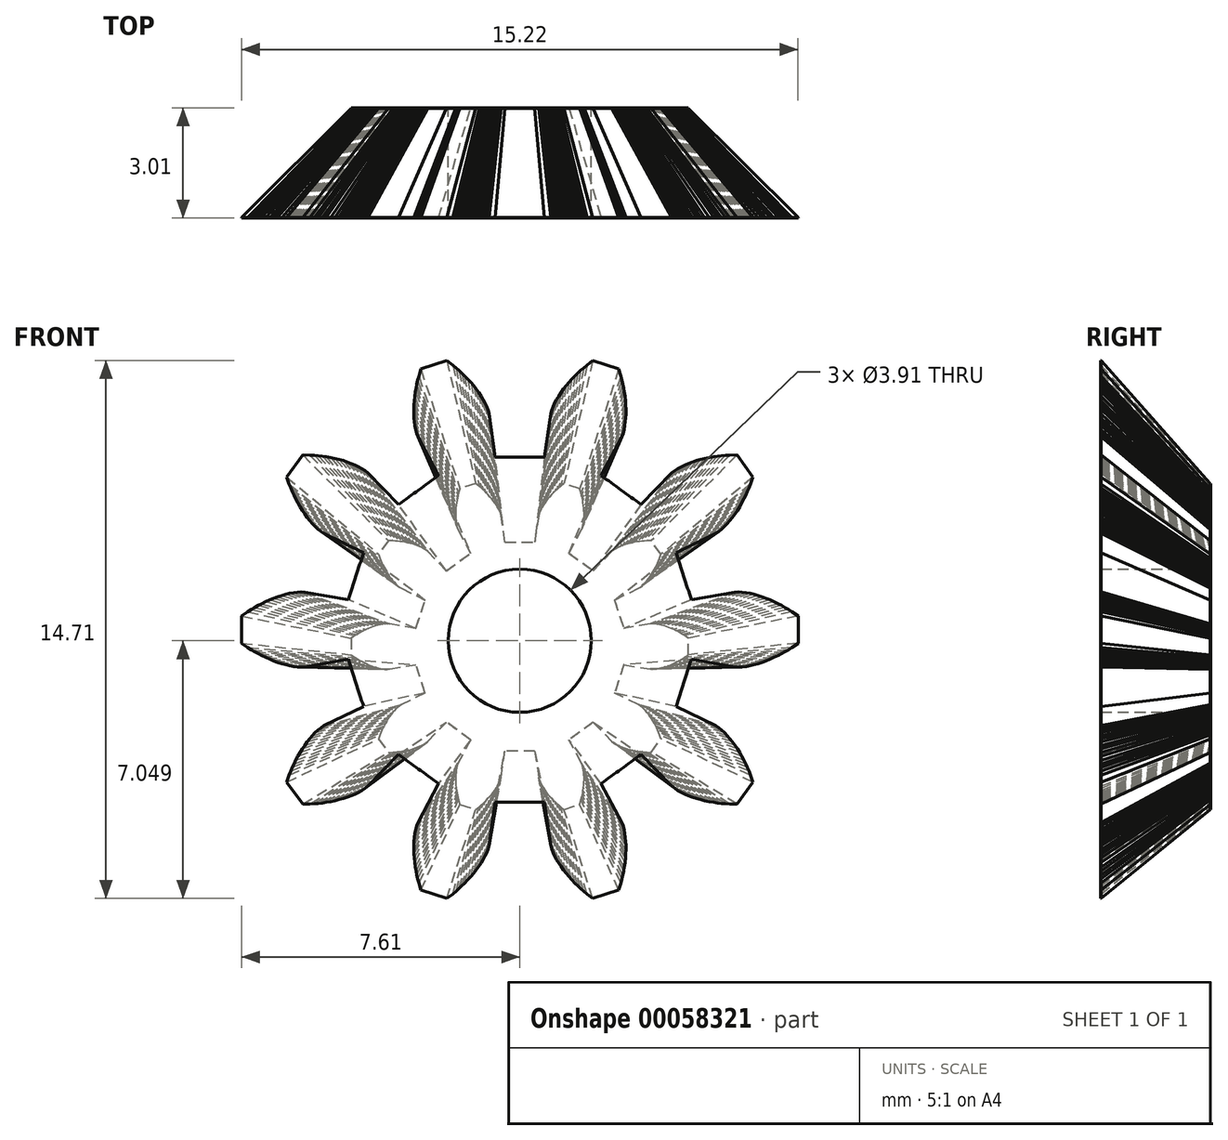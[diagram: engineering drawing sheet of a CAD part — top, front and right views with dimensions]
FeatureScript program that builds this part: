
annotation { "Feature Type Name" : "Feature", "Feature Type Description" : "" }
export const myFeature = defineFeature(function(context is Context, id is Id, definition is map)
    precondition{}
    {
        {
            var Q0;
            Q0=qCreatedBy(makeId("Front.planeOp"),FACE);
            var sketch = newSketch(context, id + "F0", { "sketchPlane" : qUnion([Q0])});
            skLineSegment(sketch, "E0", {"start": v(4.7, 0.36) * mm, "end": v(5.88, 0.15) * mm});
            skLineSegment(sketch, "E1", {"start": v(5.88, 0.15) * mm, "end": v(5.98, 0.15) * mm});
            skLineSegment(sketch, "E2", {"start": v(5.98, 0.15) * mm, "end": v(6.08, 0.15) * mm});
            skLineSegment(sketch, "E3", {"start": v(6.08, 0.15) * mm, "end": v(6.19, 0.17) * mm});
            skLineSegment(sketch, "E4", {"start": v(6.19, 0.17) * mm, "end": v(6.3, 0.19) * mm});
            skLineSegment(sketch, "E5", {"start": v(6.3, 0.19) * mm, "end": v(6.4, 0.2) * mm});
            skLineSegment(sketch, "E6", {"start": v(6.4, 0.2) * mm, "end": v(6.5, 0.24) * mm});
            skLineSegment(sketch, "E7", {"start": v(6.5, 0.24) * mm, "end": v(6.63, 0.28) * mm});
            skLineSegment(sketch, "E8", {"start": v(6.63, 0.28) * mm, "end": v(6.73, 0.32) * mm});
            skLineSegment(sketch, "E9", {"start": v(6.73, 0.32) * mm, "end": v(6.84, 0.36) * mm});
            skLineSegment(sketch, "E10", {"start": v(6.84, 0.36) * mm, "end": v(6.95, 0.4) * mm});
            skLineSegment(sketch, "E11", {"start": v(6.95, 0.4) * mm, "end": v(7.07, 0.47) * mm});
            skLineSegment(sketch, "E12", {"start": v(7.07, 0.47) * mm, "end": v(7.16, 0.52) * mm});
            skLineSegment(sketch, "E13", {"start": v(7.16, 0.52) * mm, "end": v(7.25, 0.57) * mm});
            skLineSegment(sketch, "E14", {"start": v(7.25, 0.57) * mm, "end": v(7.35, 0.63) * mm});
            skLineSegment(sketch, "E15", {"start": v(7.35, 0.63) * mm, "end": v(7.44, 0.69) * mm});
            skLineSegment(sketch, "E16", {"start": v(7.44, 0.69) * mm, "end": v(7.61, 0.8) * mm});
            skLineSegment(sketch, "E17", {"start": v(7.61, 0.8) * mm, "end": v(7.61, 1.55) * mm});
            skLineSegment(sketch, "E18", {"start": v(7.61, 1.55) * mm, "end": v(7.44, 1.66) * mm});
            skLineSegment(sketch, "E19", {"start": v(7.44, 1.66) * mm, "end": v(7.35, 1.72) * mm});
            skLineSegment(sketch, "E20", {"start": v(7.35, 1.72) * mm, "end": v(7.25, 1.78) * mm});
            skLineSegment(sketch, "E21", {"start": v(7.25, 1.78) * mm, "end": v(7.16, 1.83) * mm});
            skLineSegment(sketch, "E22", {"start": v(7.16, 1.83) * mm, "end": v(7.07, 1.88) * mm});
            skLineSegment(sketch, "E23", {"start": v(7.07, 1.88) * mm, "end": v(6.95, 1.94) * mm});
            skLineSegment(sketch, "E24", {"start": v(6.95, 1.94) * mm, "end": v(6.84, 1.99) * mm});
            skLineSegment(sketch, "E25", {"start": v(6.84, 1.99) * mm, "end": v(6.73, 2.03) * mm});
            skLineSegment(sketch, "E26", {"start": v(6.73, 2.03) * mm, "end": v(6.63, 2.07) * mm});
            skLineSegment(sketch, "E27", {"start": v(6.63, 2.07) * mm, "end": v(6.5, 2.1) * mm});
            skLineSegment(sketch, "E28", {"start": v(6.5, 2.1) * mm, "end": v(6.4, 2.14) * mm});
            skLineSegment(sketch, "E29", {"start": v(6.4, 2.14) * mm, "end": v(6.3, 2.16) * mm});
            skLineSegment(sketch, "E30", {"start": v(6.3, 2.16) * mm, "end": v(6.19, 2.18) * mm});
            skLineSegment(sketch, "E31", {"start": v(6.19, 2.18) * mm, "end": v(6.08, 2.2) * mm});
            skLineSegment(sketch, "E32", {"start": v(6.08, 2.2) * mm, "end": v(5.98, 2.2) * mm});
            skLineSegment(sketch, "E33", {"start": v(5.98, 2.2) * mm, "end": v(5.88, 2.2) * mm});
            skLineSegment(sketch, "E34", {"start": v(5.88, 2.2) * mm, "end": v(4.7, 1.99) * mm});
            skArc(sketch, "E35", {"start": v(4.7, 1.99) * mm, "mid": v(4.48, 2.63) * mm, "end": v(4.28, 3.27) * mm});
            skLineSegment(sketch, "E36", {"start": v(4.28, 3.27) * mm, "end": v(5.36, 3.8) * mm});
            skLineSegment(sketch, "E37", {"start": v(5.36, 3.8) * mm, "end": v(5.44, 3.86) * mm});
            skLineSegment(sketch, "E38", {"start": v(5.44, 3.86) * mm, "end": v(5.52, 3.92) * mm});
            skLineSegment(sketch, "E39", {"start": v(5.52, 3.92) * mm, "end": v(5.6, 4) * mm});
            skLineSegment(sketch, "E40", {"start": v(5.6, 4) * mm, "end": v(5.67, 4.08) * mm});
            skLineSegment(sketch, "E41", {"start": v(5.67, 4.08) * mm, "end": v(5.74, 4.15) * mm});
            skLineSegment(sketch, "E42", {"start": v(5.74, 4.15) * mm, "end": v(5.81, 4.24) * mm});
            skLineSegment(sketch, "E43", {"start": v(5.81, 4.24) * mm, "end": v(5.89, 4.34) * mm});
            skLineSegment(sketch, "E44", {"start": v(5.89, 4.34) * mm, "end": v(5.95, 4.44) * mm});
            skLineSegment(sketch, "E45", {"start": v(5.95, 4.44) * mm, "end": v(6.01, 4.53) * mm});
            skLineSegment(sketch, "E46", {"start": v(6.01, 4.53) * mm, "end": v(6.07, 4.64) * mm});
            skLineSegment(sketch, "E47", {"start": v(6.07, 4.64) * mm, "end": v(6.13, 4.76) * mm});
            skLineSegment(sketch, "E48", {"start": v(6.13, 4.76) * mm, "end": v(6.18, 4.85) * mm});
            skLineSegment(sketch, "E49", {"start": v(6.18, 4.85) * mm, "end": v(6.22, 4.95) * mm});
            skLineSegment(sketch, "E50", {"start": v(6.22, 4.95) * mm, "end": v(6.27, 5.05) * mm});
            skLineSegment(sketch, "E51", {"start": v(6.27, 5.05) * mm, "end": v(6.3, 5.16) * mm});
            skLineSegment(sketch, "E52", {"start": v(6.3, 5.16) * mm, "end": v(6.38, 5.35) * mm});
            skLineSegment(sketch, "E53", {"start": v(6.38, 5.35) * mm, "end": v(5.94, 5.95) * mm});
            skLineSegment(sketch, "E54", {"start": v(5.94, 5.95) * mm, "end": v(5.74, 5.94) * mm});
            skLineSegment(sketch, "E55", {"start": v(5.74, 5.94) * mm, "end": v(5.62, 5.94) * mm});
            skLineSegment(sketch, "E56", {"start": v(5.62, 5.94) * mm, "end": v(5.51, 5.93) * mm});
            skLineSegment(sketch, "E57", {"start": v(5.51, 5.93) * mm, "end": v(5.4, 5.92) * mm});
            skLineSegment(sketch, "E58", {"start": v(5.4, 5.92) * mm, "end": v(5.3, 5.9) * mm});
            skLineSegment(sketch, "E59", {"start": v(5.3, 5.9) * mm, "end": v(5.17, 5.88) * mm});
            skLineSegment(sketch, "E60", {"start": v(5.17, 5.88) * mm, "end": v(5.05, 5.85) * mm});
            skLineSegment(sketch, "E61", {"start": v(5.05, 5.85) * mm, "end": v(4.94, 5.83) * mm});
            skLineSegment(sketch, "E62", {"start": v(4.94, 5.83) * mm, "end": v(4.83, 5.8) * mm});
            skLineSegment(sketch, "E63", {"start": v(4.83, 5.8) * mm, "end": v(4.71, 5.76) * mm});
            skLineSegment(sketch, "E64", {"start": v(4.71, 5.76) * mm, "end": v(4.6, 5.72) * mm});
            skLineSegment(sketch, "E65", {"start": v(4.6, 5.72) * mm, "end": v(4.51, 5.68) * mm});
            skLineSegment(sketch, "E66", {"start": v(4.51, 5.68) * mm, "end": v(4.41, 5.63) * mm});
            skLineSegment(sketch, "E67", {"start": v(4.41, 5.63) * mm, "end": v(4.32, 5.58) * mm});
            skLineSegment(sketch, "E68", {"start": v(4.32, 5.58) * mm, "end": v(4.23, 5.52) * mm});
            skLineSegment(sketch, "E69", {"start": v(4.23, 5.52) * mm, "end": v(4.16, 5.46) * mm});
            skLineSegment(sketch, "E70", {"start": v(4.16, 5.46) * mm, "end": v(3.32, 4.6) * mm});
            skArc(sketch, "E71", {"start": v(3.32, 4.6) * mm, "mid": v(2.77, 4.99) * mm, "end": v(2.23, 5.39) * mm});
            skLineSegment(sketch, "E72", {"start": v(2.23, 5.39) * mm, "end": v(2.79, 6.45) * mm});
            skLineSegment(sketch, "E73", {"start": v(2.79, 6.45) * mm, "end": v(2.82, 6.54) * mm});
            skLineSegment(sketch, "E74", {"start": v(2.82, 6.54) * mm, "end": v(2.85, 6.64) * mm});
            skLineSegment(sketch, "E75", {"start": v(2.85, 6.64) * mm, "end": v(2.87, 6.75) * mm});
            skLineSegment(sketch, "E76", {"start": v(2.87, 6.75) * mm, "end": v(2.89, 6.86) * mm});
            skLineSegment(sketch, "E77", {"start": v(2.89, 6.86) * mm, "end": v(2.9, 6.96) * mm});
            skLineSegment(sketch, "E78", {"start": v(2.9, 6.96) * mm, "end": v(2.9, 7.07) * mm});
            skLineSegment(sketch, "E79", {"start": v(2.9, 7.07) * mm, "end": v(2.9, 7.2) * mm});
            skLineSegment(sketch, "E80", {"start": v(2.9, 7.2) * mm, "end": v(2.9, 7.3) * mm});
            skLineSegment(sketch, "E81", {"start": v(2.9, 7.3) * mm, "end": v(2.89, 7.43) * mm});
            skLineSegment(sketch, "E82", {"start": v(2.89, 7.43) * mm, "end": v(2.87, 7.55) * mm});
            skLineSegment(sketch, "E83", {"start": v(2.87, 7.55) * mm, "end": v(2.86, 7.68) * mm});
            skLineSegment(sketch, "E84", {"start": v(2.86, 7.68) * mm, "end": v(2.84, 7.78) * mm});
            skLineSegment(sketch, "E85", {"start": v(2.84, 7.78) * mm, "end": v(2.82, 7.88) * mm});
            skLineSegment(sketch, "E86", {"start": v(2.82, 7.88) * mm, "end": v(2.8, 8) * mm});
            skLineSegment(sketch, "E87", {"start": v(2.8, 8) * mm, "end": v(2.76, 8.1) * mm});
            skLineSegment(sketch, "E88", {"start": v(2.76, 8.1) * mm, "end": v(2.7, 8.3) * mm});
            skLineSegment(sketch, "E89", {"start": v(2.7, 8.3) * mm, "end": v(2, 8.53) * mm});
            skLineSegment(sketch, "E90", {"start": v(2, 8.53) * mm, "end": v(1.84, 8.4) * mm});
            skLineSegment(sketch, "E91", {"start": v(1.84, 8.4) * mm, "end": v(1.75, 8.33) * mm});
            skLineSegment(sketch, "E92", {"start": v(1.75, 8.33) * mm, "end": v(1.66, 8.26) * mm});
            skLineSegment(sketch, "E93", {"start": v(1.66, 8.26) * mm, "end": v(1.59, 8.19) * mm});
            skLineSegment(sketch, "E94", {"start": v(1.59, 8.19) * mm, "end": v(1.51, 8.11) * mm});
            skLineSegment(sketch, "E95", {"start": v(1.51, 8.11) * mm, "end": v(1.42, 8.02) * mm});
            skLineSegment(sketch, "E96", {"start": v(1.42, 8.02) * mm, "end": v(1.34, 7.93) * mm});
            skLineSegment(sketch, "E97", {"start": v(1.34, 7.93) * mm, "end": v(1.26, 7.84) * mm});
            skLineSegment(sketch, "E98", {"start": v(1.26, 7.84) * mm, "end": v(1.2, 7.75) * mm});
            skLineSegment(sketch, "E99", {"start": v(1.2, 7.75) * mm, "end": v(1.12, 7.65) * mm});
            skLineSegment(sketch, "E100", {"start": v(1.12, 7.65) * mm, "end": v(1.06, 7.56) * mm});
            skLineSegment(sketch, "E101", {"start": v(1.06, 7.56) * mm, "end": v(1, 7.47) * mm});
            skLineSegment(sketch, "E102", {"start": v(1, 7.47) * mm, "end": v(0.95, 7.37) * mm});
            skLineSegment(sketch, "E103", {"start": v(0.95, 7.37) * mm, "end": v(0.9, 7.28) * mm});
            skLineSegment(sketch, "E104", {"start": v(0.9, 7.28) * mm, "end": v(0.87, 7.18) * mm});
            skLineSegment(sketch, "E105", {"start": v(0.87, 7.18) * mm, "end": v(0.85, 7.08) * mm});
            skLineSegment(sketch, "E106", {"start": v(0.85, 7.08) * mm, "end": v(0.67, 5.89) * mm});
            skArc(sketch, "E107", {"start": v(0.67, 5.89) * mm, "mid": v(0, 5.89) * mm, "end": v(-0.67, 5.89) * mm});
            skLineSegment(sketch, "E108", {"start": v(-0.67, 5.89) * mm, "end": v(-0.85, 7.08) * mm});
            skLineSegment(sketch, "E109", {"start": v(-0.85, 7.08) * mm, "end": v(-0.87, 7.18) * mm});
            skLineSegment(sketch, "E110", {"start": v(-0.87, 7.18) * mm, "end": v(-0.9, 7.28) * mm});
            skLineSegment(sketch, "E111", {"start": v(-0.9, 7.28) * mm, "end": v(-0.95, 7.37) * mm});
            skLineSegment(sketch, "E112", {"start": v(-0.95, 7.37) * mm, "end": v(-1, 7.47) * mm});
            skLineSegment(sketch, "E113", {"start": v(-1, 7.47) * mm, "end": v(-1.06, 7.56) * mm});
            skLineSegment(sketch, "E114", {"start": v(-1.06, 7.56) * mm, "end": v(-1.12, 7.65) * mm});
            skLineSegment(sketch, "E115", {"start": v(-1.12, 7.65) * mm, "end": v(-1.2, 7.75) * mm});
            skLineSegment(sketch, "E116", {"start": v(-1.2, 7.75) * mm, "end": v(-1.26, 7.84) * mm});
            skLineSegment(sketch, "E117", {"start": v(-1.26, 7.84) * mm, "end": v(-1.34, 7.93) * mm});
            skLineSegment(sketch, "E118", {"start": v(-1.34, 7.93) * mm, "end": v(-1.42, 8.02) * mm});
            skLineSegment(sketch, "E119", {"start": v(-1.42, 8.02) * mm, "end": v(-1.51, 8.11) * mm});
            skLineSegment(sketch, "E120", {"start": v(-1.51, 8.11) * mm, "end": v(-1.59, 8.19) * mm});
            skLineSegment(sketch, "E121", {"start": v(-1.59, 8.19) * mm, "end": v(-1.66, 8.26) * mm});
            skLineSegment(sketch, "E122", {"start": v(-1.66, 8.26) * mm, "end": v(-1.75, 8.33) * mm});
            skLineSegment(sketch, "E123", {"start": v(-1.75, 8.33) * mm, "end": v(-1.84, 8.4) * mm});
            skLineSegment(sketch, "E124", {"start": v(-1.84, 8.4) * mm, "end": v(-2, 8.53) * mm});
            skLineSegment(sketch, "E125", {"start": v(-2, 8.53) * mm, "end": v(-2.7, 8.3) * mm});
            skLineSegment(sketch, "E126", {"start": v(-2.7, 8.3) * mm, "end": v(-2.76, 8.1) * mm});
            skLineSegment(sketch, "E127", {"start": v(-2.76, 8.1) * mm, "end": v(-2.8, 8) * mm});
            skLineSegment(sketch, "E128", {"start": v(-2.8, 8) * mm, "end": v(-2.82, 7.88) * mm});
            skLineSegment(sketch, "E129", {"start": v(-2.82, 7.88) * mm, "end": v(-2.84, 7.78) * mm});
            skLineSegment(sketch, "E130", {"start": v(-2.84, 7.78) * mm, "end": v(-2.86, 7.68) * mm});
            skLineSegment(sketch, "E131", {"start": v(-2.86, 7.68) * mm, "end": v(-2.87, 7.55) * mm});
            skLineSegment(sketch, "E132", {"start": v(-2.87, 7.55) * mm, "end": v(-2.89, 7.43) * mm});
            skLineSegment(sketch, "E133", {"start": v(-2.89, 7.43) * mm, "end": v(-2.9, 7.3) * mm});
            skLineSegment(sketch, "E134", {"start": v(-2.9, 7.3) * mm, "end": v(-2.9, 7.2) * mm});
            skLineSegment(sketch, "E135", {"start": v(-2.9, 7.2) * mm, "end": v(-2.9, 7.07) * mm});
            skLineSegment(sketch, "E136", {"start": v(-2.9, 7.07) * mm, "end": v(-2.9, 6.96) * mm});
            skLineSegment(sketch, "E137", {"start": v(-2.9, 6.96) * mm, "end": v(-2.89, 6.86) * mm});
            skLineSegment(sketch, "E138", {"start": v(-2.89, 6.86) * mm, "end": v(-2.87, 6.75) * mm});
            skLineSegment(sketch, "E139", {"start": v(-2.87, 6.75) * mm, "end": v(-2.85, 6.64) * mm});
            skLineSegment(sketch, "E140", {"start": v(-2.85, 6.64) * mm, "end": v(-2.82, 6.54) * mm});
            skLineSegment(sketch, "E141", {"start": v(-2.82, 6.54) * mm, "end": v(-2.79, 6.45) * mm});
            skLineSegment(sketch, "E142", {"start": v(-2.79, 6.45) * mm, "end": v(-2.23, 5.39) * mm});
            skArc(sketch, "E143", {"start": v(-2.23, 5.39) * mm, "mid": v(-2.77, 4.99) * mm, "end": v(-3.32, 4.6) * mm});
            skLineSegment(sketch, "E144", {"start": v(-3.32, 4.6) * mm, "end": v(-4.16, 5.46) * mm});
            skLineSegment(sketch, "E145", {"start": v(-4.16, 5.46) * mm, "end": v(-4.23, 5.52) * mm});
            skLineSegment(sketch, "E146", {"start": v(-4.23, 5.52) * mm, "end": v(-4.32, 5.58) * mm});
            skLineSegment(sketch, "E147", {"start": v(-4.32, 5.58) * mm, "end": v(-4.41, 5.63) * mm});
            skLineSegment(sketch, "E148", {"start": v(-4.41, 5.63) * mm, "end": v(-4.51, 5.68) * mm});
            skLineSegment(sketch, "E149", {"start": v(-4.51, 5.68) * mm, "end": v(-4.6, 5.72) * mm});
            skLineSegment(sketch, "E150", {"start": v(-4.6, 5.72) * mm, "end": v(-4.71, 5.76) * mm});
            skLineSegment(sketch, "E151", {"start": v(-4.71, 5.76) * mm, "end": v(-4.83, 5.8) * mm});
            skLineSegment(sketch, "E152", {"start": v(-4.83, 5.8) * mm, "end": v(-4.94, 5.83) * mm});
            skLineSegment(sketch, "E153", {"start": v(-4.94, 5.83) * mm, "end": v(-5.05, 5.85) * mm});
            skLineSegment(sketch, "E154", {"start": v(-5.05, 5.85) * mm, "end": v(-5.17, 5.88) * mm});
            skLineSegment(sketch, "E155", {"start": v(-5.17, 5.88) * mm, "end": v(-5.3, 5.9) * mm});
            skLineSegment(sketch, "E156", {"start": v(-5.3, 5.9) * mm, "end": v(-5.4, 5.92) * mm});
            skLineSegment(sketch, "E157", {"start": v(-5.4, 5.92) * mm, "end": v(-5.51, 5.93) * mm});
            skLineSegment(sketch, "E158", {"start": v(-5.51, 5.93) * mm, "end": v(-5.62, 5.94) * mm});
            skLineSegment(sketch, "E159", {"start": v(-5.62, 5.94) * mm, "end": v(-5.74, 5.94) * mm});
            skLineSegment(sketch, "E160", {"start": v(-5.74, 5.94) * mm, "end": v(-5.94, 5.95) * mm});
            skLineSegment(sketch, "E161", {"start": v(-5.94, 5.95) * mm, "end": v(-6.38, 5.35) * mm});
            skLineSegment(sketch, "E162", {"start": v(-6.38, 5.35) * mm, "end": v(-6.3, 5.16) * mm});
            skLineSegment(sketch, "E163", {"start": v(-6.3, 5.16) * mm, "end": v(-6.27, 5.05) * mm});
            skLineSegment(sketch, "E164", {"start": v(-6.27, 5.05) * mm, "end": v(-6.22, 4.95) * mm});
            skLineSegment(sketch, "E165", {"start": v(-6.22, 4.95) * mm, "end": v(-6.18, 4.85) * mm});
            skLineSegment(sketch, "E166", {"start": v(-6.18, 4.85) * mm, "end": v(-6.13, 4.76) * mm});
            skLineSegment(sketch, "E167", {"start": v(-6.13, 4.76) * mm, "end": v(-6.07, 4.64) * mm});
            skLineSegment(sketch, "E168", {"start": v(-6.07, 4.64) * mm, "end": v(-6.01, 4.53) * mm});
            skLineSegment(sketch, "E169", {"start": v(-6.01, 4.53) * mm, "end": v(-5.95, 4.44) * mm});
            skLineSegment(sketch, "E170", {"start": v(-5.95, 4.44) * mm, "end": v(-5.89, 4.34) * mm});
            skLineSegment(sketch, "E171", {"start": v(-5.89, 4.34) * mm, "end": v(-5.81, 4.24) * mm});
            skLineSegment(sketch, "E172", {"start": v(-5.81, 4.24) * mm, "end": v(-5.74, 4.15) * mm});
            skLineSegment(sketch, "E173", {"start": v(-5.74, 4.15) * mm, "end": v(-5.67, 4.08) * mm});
            skLineSegment(sketch, "E174", {"start": v(-5.67, 4.08) * mm, "end": v(-5.6, 4) * mm});
            skLineSegment(sketch, "E175", {"start": v(-5.6, 4) * mm, "end": v(-5.52, 3.92) * mm});
            skLineSegment(sketch, "E176", {"start": v(-5.52, 3.92) * mm, "end": v(-5.44, 3.86) * mm});
            skLineSegment(sketch, "E177", {"start": v(-5.44, 3.86) * mm, "end": v(-5.36, 3.8) * mm});
            skLineSegment(sketch, "E178", {"start": v(-5.36, 3.8) * mm, "end": v(-4.28, 3.27) * mm});
            skArc(sketch, "E179", {"start": v(-4.28, 3.27) * mm, "mid": v(-4.48, 2.63) * mm, "end": v(-4.7, 1.99) * mm});
            skLineSegment(sketch, "E180", {"start": v(-4.7, 1.99) * mm, "end": v(-5.88, 2.2) * mm});
            skLineSegment(sketch, "E181", {"start": v(-5.88, 2.2) * mm, "end": v(-5.98, 2.2) * mm});
            skLineSegment(sketch, "E182", {"start": v(-5.98, 2.2) * mm, "end": v(-6.08, 2.2) * mm});
            skLineSegment(sketch, "E183", {"start": v(-6.08, 2.2) * mm, "end": v(-6.19, 2.18) * mm});
            skLineSegment(sketch, "E184", {"start": v(-6.19, 2.18) * mm, "end": v(-6.3, 2.16) * mm});
            skLineSegment(sketch, "E185", {"start": v(-6.3, 2.16) * mm, "end": v(-6.4, 2.14) * mm});
            skLineSegment(sketch, "E186", {"start": v(-6.4, 2.14) * mm, "end": v(-6.5, 2.1) * mm});
            skLineSegment(sketch, "E187", {"start": v(-6.5, 2.1) * mm, "end": v(-6.63, 2.07) * mm});
            skLineSegment(sketch, "E188", {"start": v(-6.63, 2.07) * mm, "end": v(-6.73, 2.03) * mm});
            skLineSegment(sketch, "E189", {"start": v(-6.73, 2.03) * mm, "end": v(-6.84, 1.99) * mm});
            skLineSegment(sketch, "E190", {"start": v(-6.84, 1.99) * mm, "end": v(-6.95, 1.94) * mm});
            skLineSegment(sketch, "E191", {"start": v(-6.95, 1.94) * mm, "end": v(-7.07, 1.88) * mm});
            skLineSegment(sketch, "E192", {"start": v(-7.07, 1.88) * mm, "end": v(-7.16, 1.83) * mm});
            skLineSegment(sketch, "E193", {"start": v(-7.16, 1.83) * mm, "end": v(-7.25, 1.78) * mm});
            skLineSegment(sketch, "E194", {"start": v(-7.25, 1.78) * mm, "end": v(-7.35, 1.72) * mm});
            skLineSegment(sketch, "E195", {"start": v(-7.35, 1.72) * mm, "end": v(-7.44, 1.66) * mm});
            skLineSegment(sketch, "E196", {"start": v(-7.44, 1.66) * mm, "end": v(-7.61, 1.55) * mm});
            skLineSegment(sketch, "E197", {"start": v(-7.61, 1.55) * mm, "end": v(-7.61, 0.8) * mm});
            skLineSegment(sketch, "E198", {"start": v(-7.61, 0.8) * mm, "end": v(-7.44, 0.69) * mm});
            skLineSegment(sketch, "E199", {"start": v(-7.44, 0.69) * mm, "end": v(-7.35, 0.63) * mm});
            skLineSegment(sketch, "E200", {"start": v(-7.35, 0.63) * mm, "end": v(-7.25, 0.57) * mm});
            skLineSegment(sketch, "E201", {"start": v(-7.25, 0.57) * mm, "end": v(-7.16, 0.52) * mm});
            skLineSegment(sketch, "E202", {"start": v(-7.16, 0.52) * mm, "end": v(-7.07, 0.47) * mm});
            skLineSegment(sketch, "E203", {"start": v(-7.07, 0.47) * mm, "end": v(-6.95, 0.4) * mm});
            skLineSegment(sketch, "E204", {"start": v(-6.95, 0.4) * mm, "end": v(-6.84, 0.36) * mm});
            skLineSegment(sketch, "E205", {"start": v(-6.84, 0.36) * mm, "end": v(-6.73, 0.32) * mm});
            skLineSegment(sketch, "E206", {"start": v(-6.73, 0.32) * mm, "end": v(-6.63, 0.28) * mm});
            skLineSegment(sketch, "E207", {"start": v(-6.63, 0.28) * mm, "end": v(-6.5, 0.24) * mm});
            skLineSegment(sketch, "E208", {"start": v(-6.5, 0.24) * mm, "end": v(-6.4, 0.2) * mm});
            skLineSegment(sketch, "E209", {"start": v(-6.4, 0.2) * mm, "end": v(-6.3, 0.19) * mm});
            skLineSegment(sketch, "E210", {"start": v(-6.3, 0.19) * mm, "end": v(-6.19, 0.17) * mm});
            skLineSegment(sketch, "E211", {"start": v(-6.19, 0.17) * mm, "end": v(-6.08, 0.15) * mm});
            skLineSegment(sketch, "E212", {"start": v(-6.08, 0.15) * mm, "end": v(-5.98, 0.15) * mm});
            skLineSegment(sketch, "E213", {"start": v(-5.98, 0.15) * mm, "end": v(-5.88, 0.15) * mm});
            skLineSegment(sketch, "E214", {"start": v(-5.88, 0.15) * mm, "end": v(-4.7, 0.36) * mm});
            skArc(sketch, "E215", {"start": v(-4.7, 0.36) * mm, "mid": v(-4.48, -0.28) * mm, "end": v(-4.28, -0.92) * mm});
            skLineSegment(sketch, "E216", {"start": v(-4.28, -0.92) * mm, "end": v(-5.36, -1.45) * mm});
            skLineSegment(sketch, "E217", {"start": v(-5.36, -1.45) * mm, "end": v(-5.44, -1.5) * mm});
            skLineSegment(sketch, "E218", {"start": v(-5.44, -1.5) * mm, "end": v(-5.52, -1.57) * mm});
            skLineSegment(sketch, "E219", {"start": v(-5.52, -1.57) * mm, "end": v(-5.6, -1.65) * mm});
            skLineSegment(sketch, "E220", {"start": v(-5.6, -1.65) * mm, "end": v(-5.67, -1.73) * mm});
            skLineSegment(sketch, "E221", {"start": v(-5.67, -1.73) * mm, "end": v(-5.74, -1.8) * mm});
            skLineSegment(sketch, "E222", {"start": v(-5.74, -1.8) * mm, "end": v(-5.81, -1.9) * mm});
            skLineSegment(sketch, "E223", {"start": v(-5.81, -1.9) * mm, "end": v(-5.89, -2) * mm});
            skLineSegment(sketch, "E224", {"start": v(-5.89, -2) * mm, "end": v(-5.95, -2.09) * mm});
            skLineSegment(sketch, "E225", {"start": v(-5.95, -2.09) * mm, "end": v(-6.01, -2.18) * mm});
            skLineSegment(sketch, "E226", {"start": v(-6.01, -2.18) * mm, "end": v(-6.07, -2.3) * mm});
            skLineSegment(sketch, "E227", {"start": v(-6.07, -2.3) * mm, "end": v(-6.13, -2.4) * mm});
            skLineSegment(sketch, "E228", {"start": v(-6.13, -2.4) * mm, "end": v(-6.18, -2.5) * mm});
            skLineSegment(sketch, "E229", {"start": v(-6.18, -2.5) * mm, "end": v(-6.22, -2.6) * mm});
            skLineSegment(sketch, "E230", {"start": v(-6.22, -2.6) * mm, "end": v(-6.27, -2.7) * mm});
            skLineSegment(sketch, "E231", {"start": v(-6.27, -2.7) * mm, "end": v(-6.3, -2.8) * mm});
            skLineSegment(sketch, "E232", {"start": v(-6.3, -2.8) * mm, "end": v(-6.38, -3) * mm});
            skLineSegment(sketch, "E233", {"start": v(-6.38, -3) * mm, "end": v(-5.94, -3.6) * mm});
            skLineSegment(sketch, "E234", {"start": v(-5.94, -3.6) * mm, "end": v(-5.74, -3.6) * mm});
            skLineSegment(sketch, "E235", {"start": v(-5.74, -3.6) * mm, "end": v(-5.62, -3.59) * mm});
            skLineSegment(sketch, "E236", {"start": v(-5.62, -3.59) * mm, "end": v(-5.51, -3.58) * mm});
            skLineSegment(sketch, "E237", {"start": v(-5.51, -3.58) * mm, "end": v(-5.4, -3.57) * mm});
            skLineSegment(sketch, "E238", {"start": v(-5.4, -3.57) * mm, "end": v(-5.3, -3.55) * mm});
            skLineSegment(sketch, "E239", {"start": v(-5.3, -3.55) * mm, "end": v(-5.17, -3.53) * mm});
            skLineSegment(sketch, "E240", {"start": v(-5.17, -3.53) * mm, "end": v(-5.05, -3.5) * mm});
            skLineSegment(sketch, "E241", {"start": v(-5.05, -3.5) * mm, "end": v(-4.94, -3.48) * mm});
            skLineSegment(sketch, "E242", {"start": v(-4.94, -3.48) * mm, "end": v(-4.83, -3.45) * mm});
            skLineSegment(sketch, "E243", {"start": v(-4.83, -3.45) * mm, "end": v(-4.71, -3.4) * mm});
            skLineSegment(sketch, "E244", {"start": v(-4.71, -3.4) * mm, "end": v(-4.6, -3.37) * mm});
            skLineSegment(sketch, "E245", {"start": v(-4.6, -3.37) * mm, "end": v(-4.51, -3.33) * mm});
            skLineSegment(sketch, "E246", {"start": v(-4.51, -3.33) * mm, "end": v(-4.41, -3.28) * mm});
            skLineSegment(sketch, "E247", {"start": v(-4.41, -3.28) * mm, "end": v(-4.32, -3.23) * mm});
            skLineSegment(sketch, "E248", {"start": v(-4.32, -3.23) * mm, "end": v(-4.23, -3.17) * mm});
            skLineSegment(sketch, "E249", {"start": v(-4.23, -3.17) * mm, "end": v(-4.16, -3.1) * mm});
            skLineSegment(sketch, "E250", {"start": v(-4.16, -3.1) * mm, "end": v(-3.32, -2.24) * mm});
            skArc(sketch, "E251", {"start": v(-3.32, -2.24) * mm, "mid": v(-2.77, -2.64) * mm, "end": v(-2.23, -3.04) * mm});
            skLineSegment(sketch, "E252", {"start": v(-2.23, -3.04) * mm, "end": v(-2.79, -4.1) * mm});
            skLineSegment(sketch, "E253", {"start": v(-2.79, -4.1) * mm, "end": v(-2.82, -4.2) * mm});
            skLineSegment(sketch, "E254", {"start": v(-2.82, -4.2) * mm, "end": v(-2.85, -4.3) * mm});
            skLineSegment(sketch, "E255", {"start": v(-2.85, -4.3) * mm, "end": v(-2.87, -4.4) * mm});
            skLineSegment(sketch, "E256", {"start": v(-2.87, -4.4) * mm, "end": v(-2.89, -4.5) * mm});
            skLineSegment(sketch, "E257", {"start": v(-2.89, -4.5) * mm, "end": v(-2.9, -4.61) * mm});
            skLineSegment(sketch, "E258", {"start": v(-2.9, -4.61) * mm, "end": v(-2.9, -4.73) * mm});
            skLineSegment(sketch, "E259", {"start": v(-2.9, -4.73) * mm, "end": v(-2.9, -4.85) * mm});
            skLineSegment(sketch, "E260", {"start": v(-2.9, -4.85) * mm, "end": v(-2.9, -4.96) * mm});
            skLineSegment(sketch, "E261", {"start": v(-2.9, -4.96) * mm, "end": v(-2.89, -5.08) * mm});
            skLineSegment(sketch, "E262", {"start": v(-2.89, -5.08) * mm, "end": v(-2.87, -5.2) * mm});
            skLineSegment(sketch, "E263", {"start": v(-2.87, -5.2) * mm, "end": v(-2.86, -5.33) * mm});
            skLineSegment(sketch, "E264", {"start": v(-2.86, -5.33) * mm, "end": v(-2.84, -5.43) * mm});
            skLineSegment(sketch, "E265", {"start": v(-2.84, -5.43) * mm, "end": v(-2.82, -5.54) * mm});
            skLineSegment(sketch, "E266", {"start": v(-2.82, -5.54) * mm, "end": v(-2.8, -5.64) * mm});
            skLineSegment(sketch, "E267", {"start": v(-2.8, -5.64) * mm, "end": v(-2.76, -5.76) * mm});
            skLineSegment(sketch, "E268", {"start": v(-2.76, -5.76) * mm, "end": v(-2.7, -5.95) * mm});
            skLineSegment(sketch, "E269", {"start": v(-2.7, -5.95) * mm, "end": v(-2, -6.18) * mm});
            skLineSegment(sketch, "E270", {"start": v(-2, -6.18) * mm, "end": v(-1.84, -6.06) * mm});
            skLineSegment(sketch, "E271", {"start": v(-1.84, -6.06) * mm, "end": v(-1.75, -5.98) * mm});
            skLineSegment(sketch, "E272", {"start": v(-1.75, -5.98) * mm, "end": v(-1.66, -5.9) * mm});
            skLineSegment(sketch, "E273", {"start": v(-1.66, -5.9) * mm, "end": v(-1.59, -5.84) * mm});
            skLineSegment(sketch, "E274", {"start": v(-1.59, -5.84) * mm, "end": v(-1.51, -5.77) * mm});
            skLineSegment(sketch, "E275", {"start": v(-1.51, -5.77) * mm, "end": v(-1.42, -5.67) * mm});
            skLineSegment(sketch, "E276", {"start": v(-1.42, -5.67) * mm, "end": v(-1.34, -5.58) * mm});
            skLineSegment(sketch, "E277", {"start": v(-1.34, -5.58) * mm, "end": v(-1.26, -5.5) * mm});
            skLineSegment(sketch, "E278", {"start": v(-1.26, -5.5) * mm, "end": v(-1.2, -5.4) * mm});
            skLineSegment(sketch, "E279", {"start": v(-1.2, -5.4) * mm, "end": v(-1.12, -5.3) * mm});
            skLineSegment(sketch, "E280", {"start": v(-1.12, -5.3) * mm, "end": v(-1.06, -5.2) * mm});
            skLineSegment(sketch, "E281", {"start": v(-1.06, -5.2) * mm, "end": v(-1, -5.12) * mm});
            skLineSegment(sketch, "E282", {"start": v(-1, -5.12) * mm, "end": v(-0.95, -5.02) * mm});
            skLineSegment(sketch, "E283", {"start": v(-0.95, -5.02) * mm, "end": v(-0.9, -4.93) * mm});
            skLineSegment(sketch, "E284", {"start": v(-0.9, -4.93) * mm, "end": v(-0.87, -4.83) * mm});
            skLineSegment(sketch, "E285", {"start": v(-0.87, -4.83) * mm, "end": v(-0.85, -4.73) * mm});
            skLineSegment(sketch, "E286", {"start": v(-0.85, -4.73) * mm, "end": v(-0.67, -3.54) * mm});
            skArc(sketch, "E287", {"start": v(-0.67, -3.54) * mm, "mid": v(0, -3.54) * mm, "end": v(0.67, -3.54) * mm});
            skLineSegment(sketch, "E288", {"start": v(0.67, -3.54) * mm, "end": v(0.85, -4.73) * mm});
            skLineSegment(sketch, "E289", {"start": v(0.85, -4.73) * mm, "end": v(0.87, -4.83) * mm});
            skLineSegment(sketch, "E290", {"start": v(0.87, -4.83) * mm, "end": v(0.9, -4.93) * mm});
            skLineSegment(sketch, "E291", {"start": v(0.9, -4.93) * mm, "end": v(0.95, -5.02) * mm});
            skLineSegment(sketch, "E292", {"start": v(0.95, -5.02) * mm, "end": v(1, -5.12) * mm});
            skLineSegment(sketch, "E293", {"start": v(1, -5.12) * mm, "end": v(1.06, -5.2) * mm});
            skLineSegment(sketch, "E294", {"start": v(1.06, -5.2) * mm, "end": v(1.12, -5.3) * mm});
            skLineSegment(sketch, "E295", {"start": v(1.12, -5.3) * mm, "end": v(1.2, -5.4) * mm});
            skLineSegment(sketch, "E296", {"start": v(1.2, -5.4) * mm, "end": v(1.26, -5.5) * mm});
            skLineSegment(sketch, "E297", {"start": v(1.26, -5.5) * mm, "end": v(1.34, -5.58) * mm});
            skLineSegment(sketch, "E298", {"start": v(1.34, -5.58) * mm, "end": v(1.42, -5.67) * mm});
            skLineSegment(sketch, "E299", {"start": v(1.42, -5.67) * mm, "end": v(1.51, -5.77) * mm});
            skLineSegment(sketch, "E300", {"start": v(1.51, -5.77) * mm, "end": v(1.59, -5.84) * mm});
            skLineSegment(sketch, "E301", {"start": v(1.59, -5.84) * mm, "end": v(1.66, -5.9) * mm});
            skLineSegment(sketch, "E302", {"start": v(1.66, -5.9) * mm, "end": v(1.75, -5.98) * mm});
            skLineSegment(sketch, "E303", {"start": v(1.75, -5.98) * mm, "end": v(1.84, -6.06) * mm});
            skLineSegment(sketch, "E304", {"start": v(1.84, -6.06) * mm, "end": v(2, -6.18) * mm});
            skLineSegment(sketch, "E305", {"start": v(2, -6.18) * mm, "end": v(2.7, -5.95) * mm});
            skLineSegment(sketch, "E306", {"start": v(2.7, -5.95) * mm, "end": v(2.76, -5.76) * mm});
            skLineSegment(sketch, "E307", {"start": v(2.76, -5.76) * mm, "end": v(2.8, -5.64) * mm});
            skLineSegment(sketch, "E308", {"start": v(2.8, -5.64) * mm, "end": v(2.82, -5.54) * mm});
            skLineSegment(sketch, "E309", {"start": v(2.82, -5.54) * mm, "end": v(2.84, -5.43) * mm});
            skLineSegment(sketch, "E310", {"start": v(2.84, -5.43) * mm, "end": v(2.86, -5.33) * mm});
            skLineSegment(sketch, "E311", {"start": v(2.86, -5.33) * mm, "end": v(2.87, -5.2) * mm});
            skLineSegment(sketch, "E312", {"start": v(2.87, -5.2) * mm, "end": v(2.89, -5.08) * mm});
            skLineSegment(sketch, "E313", {"start": v(2.89, -5.08) * mm, "end": v(2.9, -4.96) * mm});
            skLineSegment(sketch, "E314", {"start": v(2.9, -4.96) * mm, "end": v(2.9, -4.85) * mm});
            skLineSegment(sketch, "E315", {"start": v(2.9, -4.85) * mm, "end": v(2.9, -4.73) * mm});
            skLineSegment(sketch, "E316", {"start": v(2.9, -4.73) * mm, "end": v(2.9, -4.61) * mm});
            skLineSegment(sketch, "E317", {"start": v(2.9, -4.61) * mm, "end": v(2.89, -4.5) * mm});
            skLineSegment(sketch, "E318", {"start": v(2.89, -4.5) * mm, "end": v(2.87, -4.4) * mm});
            skLineSegment(sketch, "E319", {"start": v(2.87, -4.4) * mm, "end": v(2.85, -4.3) * mm});
            skLineSegment(sketch, "E320", {"start": v(2.85, -4.3) * mm, "end": v(2.82, -4.2) * mm});
            skLineSegment(sketch, "E321", {"start": v(2.82, -4.2) * mm, "end": v(2.79, -4.1) * mm});
            skLineSegment(sketch, "E322", {"start": v(2.79, -4.1) * mm, "end": v(2.23, -3.04) * mm});
            skArc(sketch, "E323", {"start": v(2.23, -3.04) * mm, "mid": v(2.77, -2.64) * mm, "end": v(3.32, -2.24) * mm});
            skLineSegment(sketch, "E324", {"start": v(3.32, -2.24) * mm, "end": v(4.16, -3.1) * mm});
            skLineSegment(sketch, "E325", {"start": v(4.16, -3.1) * mm, "end": v(4.23, -3.17) * mm});
            skLineSegment(sketch, "E326", {"start": v(4.23, -3.17) * mm, "end": v(4.32, -3.23) * mm});
            skLineSegment(sketch, "E327", {"start": v(4.32, -3.23) * mm, "end": v(4.41, -3.28) * mm});
            skLineSegment(sketch, "E328", {"start": v(4.41, -3.28) * mm, "end": v(4.51, -3.33) * mm});
            skLineSegment(sketch, "E329", {"start": v(4.51, -3.33) * mm, "end": v(4.6, -3.37) * mm});
            skLineSegment(sketch, "E330", {"start": v(4.6, -3.37) * mm, "end": v(4.71, -3.4) * mm});
            skLineSegment(sketch, "E331", {"start": v(4.71, -3.4) * mm, "end": v(4.83, -3.45) * mm});
            skLineSegment(sketch, "E332", {"start": v(4.83, -3.45) * mm, "end": v(4.94, -3.48) * mm});
            skLineSegment(sketch, "E333", {"start": v(4.94, -3.48) * mm, "end": v(5.05, -3.5) * mm});
            skLineSegment(sketch, "E334", {"start": v(5.05, -3.5) * mm, "end": v(5.17, -3.53) * mm});
            skLineSegment(sketch, "E335", {"start": v(5.17, -3.53) * mm, "end": v(5.3, -3.55) * mm});
            skLineSegment(sketch, "E336", {"start": v(5.3, -3.55) * mm, "end": v(5.4, -3.57) * mm});
            skLineSegment(sketch, "E337", {"start": v(5.4, -3.57) * mm, "end": v(5.51, -3.58) * mm});
            skLineSegment(sketch, "E338", {"start": v(5.51, -3.58) * mm, "end": v(5.62, -3.59) * mm});
            skLineSegment(sketch, "E339", {"start": v(5.62, -3.59) * mm, "end": v(5.74, -3.6) * mm});
            skLineSegment(sketch, "E340", {"start": v(5.74, -3.6) * mm, "end": v(5.94, -3.6) * mm});
            skLineSegment(sketch, "E341", {"start": v(5.94, -3.6) * mm, "end": v(6.38, -3) * mm});
            skLineSegment(sketch, "E342", {"start": v(6.38, -3) * mm, "end": v(6.3, -2.8) * mm});
            skLineSegment(sketch, "E343", {"start": v(6.3, -2.8) * mm, "end": v(6.27, -2.7) * mm});
            skLineSegment(sketch, "E344", {"start": v(6.27, -2.7) * mm, "end": v(6.22, -2.6) * mm});
            skLineSegment(sketch, "E345", {"start": v(6.22, -2.6) * mm, "end": v(6.18, -2.5) * mm});
            skLineSegment(sketch, "E346", {"start": v(6.18, -2.5) * mm, "end": v(6.13, -2.4) * mm});
            skLineSegment(sketch, "E347", {"start": v(6.13, -2.4) * mm, "end": v(6.07, -2.3) * mm});
            skLineSegment(sketch, "E348", {"start": v(6.07, -2.3) * mm, "end": v(6.01, -2.18) * mm});
            skLineSegment(sketch, "E349", {"start": v(6.01, -2.18) * mm, "end": v(5.95, -2.09) * mm});
            skLineSegment(sketch, "E350", {"start": v(5.95, -2.09) * mm, "end": v(5.89, -2) * mm});
            skLineSegment(sketch, "E351", {"start": v(5.89, -2) * mm, "end": v(5.81, -1.9) * mm});
            skLineSegment(sketch, "E352", {"start": v(5.81, -1.9) * mm, "end": v(5.74, -1.8) * mm});
            skLineSegment(sketch, "E353", {"start": v(5.74, -1.8) * mm, "end": v(5.67, -1.73) * mm});
            skLineSegment(sketch, "E354", {"start": v(5.67, -1.73) * mm, "end": v(5.6, -1.65) * mm});
            skLineSegment(sketch, "E355", {"start": v(5.6, -1.65) * mm, "end": v(5.52, -1.57) * mm});
            skLineSegment(sketch, "E356", {"start": v(5.52, -1.57) * mm, "end": v(5.44, -1.5) * mm});
            skLineSegment(sketch, "E357", {"start": v(5.44, -1.5) * mm, "end": v(5.36, -1.45) * mm});
            skLineSegment(sketch, "E358", {"start": v(5.36, -1.45) * mm, "end": v(4.28, -0.92) * mm});
            skArc(sketch, "E359", {"start": v(4.28, -0.92) * mm, "mid": v(4.48, -0.28) * mm, "end": v(4.7, 0.36) * mm});
            skSolve(sketch);
        }
        {
            var Q0;
            Q0 = qSketchRegion(id + "F0", true);
            extrude(context, id + "F1", {"entities" : qUnion([Q0]), "depth" : 0.01 * mm});
        }
        {
            var Q0;
            Q0=makeQuery(id+"F1.opExtrude","SWEPT_BODY",BODY,{"disambiguationData":[OSD([sQuery(id+"F0.wireOp",EDGE,"E0"),sQuery(id+"F0.wireOp",EDGE,"E1"),sQuery(id+"F0.wireOp",EDGE,"E2"),sQuery(id+"F0.wireOp",EDGE,"E3"),sQuery(id+"F0.wireOp",EDGE,"E4"),sQuery(id+"F0.wireOp",EDGE,"E5"),sQuery(id+"F0.wireOp",EDGE,"E6"),sQuery(id+"F0.wireOp",EDGE,"E7"),sQuery(id+"F0.wireOp",EDGE,"E8"),sQuery(id+"F0.wireOp",EDGE,"E9"),sQuery(id+"F0.wireOp",EDGE,"E10"),sQuery(id+"F0.wireOp",EDGE,"E11"),sQuery(id+"F0.wireOp",EDGE,"E12"),sQuery(id+"F0.wireOp",EDGE,"E13"),sQuery(id+"F0.wireOp",EDGE,"E14"),sQuery(id+"F0.wireOp",EDGE,"E15"),sQuery(id+"F0.wireOp",EDGE,"E16"),sQuery(id+"F0.wireOp",EDGE,"E17"),sQuery(id+"F0.wireOp",EDGE,"E18"),sQuery(id+"F0.wireOp",EDGE,"E19"),sQuery(id+"F0.wireOp",EDGE,"E20"),sQuery(id+"F0.wireOp",EDGE,"E21"),sQuery(id+"F0.wireOp",EDGE,"E22"),sQuery(id+"F0.wireOp",EDGE,"E23"),sQuery(id+"F0.wireOp",EDGE,"E24"),sQuery(id+"F0.wireOp",EDGE,"E25"),sQuery(id+"F0.wireOp",EDGE,"E26"),sQuery(id+"F0.wireOp",EDGE,"E27"),sQuery(id+"F0.wireOp",EDGE,"E28"),sQuery(id+"F0.wireOp",EDGE,"E29"),sQuery(id+"F0.wireOp",EDGE,"E30"),sQuery(id+"F0.wireOp",EDGE,"E31"),sQuery(id+"F0.wireOp",EDGE,"E32"),sQuery(id+"F0.wireOp",EDGE,"E33"),sQuery(id+"F0.wireOp",EDGE,"E34"),sQuery(id+"F0.wireOp",EDGE,"E35"),sQuery(id+"F0.wireOp",EDGE,"E36"),sQuery(id+"F0.wireOp",EDGE,"E37"),sQuery(id+"F0.wireOp",EDGE,"E38"),sQuery(id+"F0.wireOp",EDGE,"E39"),sQuery(id+"F0.wireOp",EDGE,"E40"),sQuery(id+"F0.wireOp",EDGE,"E41"),sQuery(id+"F0.wireOp",EDGE,"E42"),sQuery(id+"F0.wireOp",EDGE,"E43"),sQuery(id+"F0.wireOp",EDGE,"E44"),sQuery(id+"F0.wireOp",EDGE,"E45"),sQuery(id+"F0.wireOp",EDGE,"E46"),sQuery(id+"F0.wireOp",EDGE,"E47"),sQuery(id+"F0.wireOp",EDGE,"E48"),sQuery(id+"F0.wireOp",EDGE,"E49"),sQuery(id+"F0.wireOp",EDGE,"E50"),sQuery(id+"F0.wireOp",EDGE,"E51"),sQuery(id+"F0.wireOp",EDGE,"E52"),sQuery(id+"F0.wireOp",EDGE,"E53"),sQuery(id+"F0.wireOp",EDGE,"E54"),sQuery(id+"F0.wireOp",EDGE,"E55"),sQuery(id+"F0.wireOp",EDGE,"E56"),sQuery(id+"F0.wireOp",EDGE,"E57"),sQuery(id+"F0.wireOp",EDGE,"E58"),sQuery(id+"F0.wireOp",EDGE,"E59"),sQuery(id+"F0.wireOp",EDGE,"E60"),sQuery(id+"F0.wireOp",EDGE,"E61"),sQuery(id+"F0.wireOp",EDGE,"E62"),sQuery(id+"F0.wireOp",EDGE,"E63"),sQuery(id+"F0.wireOp",EDGE,"E64"),sQuery(id+"F0.wireOp",EDGE,"E65"),sQuery(id+"F0.wireOp",EDGE,"E66"),sQuery(id+"F0.wireOp",EDGE,"E67"),sQuery(id+"F0.wireOp",EDGE,"E68"),sQuery(id+"F0.wireOp",EDGE,"E69"),sQuery(id+"F0.wireOp",EDGE,"E70"),sQuery(id+"F0.wireOp",EDGE,"E71"),sQuery(id+"F0.wireOp",EDGE,"E72"),sQuery(id+"F0.wireOp",EDGE,"E73"),sQuery(id+"F0.wireOp",EDGE,"E74"),sQuery(id+"F0.wireOp",EDGE,"E75"),sQuery(id+"F0.wireOp",EDGE,"E76"),sQuery(id+"F0.wireOp",EDGE,"E77"),sQuery(id+"F0.wireOp",EDGE,"E78"),sQuery(id+"F0.wireOp",EDGE,"E79"),sQuery(id+"F0.wireOp",EDGE,"E80"),sQuery(id+"F0.wireOp",EDGE,"E81"),sQuery(id+"F0.wireOp",EDGE,"E82"),sQuery(id+"F0.wireOp",EDGE,"E83"),sQuery(id+"F0.wireOp",EDGE,"E84"),sQuery(id+"F0.wireOp",EDGE,"E85"),sQuery(id+"F0.wireOp",EDGE,"E86"),sQuery(id+"F0.wireOp",EDGE,"E87"),sQuery(id+"F0.wireOp",EDGE,"E88"),sQuery(id+"F0.wireOp",EDGE,"E89"),sQuery(id+"F0.wireOp",EDGE,"E90"),sQuery(id+"F0.wireOp",EDGE,"E91"),sQuery(id+"F0.wireOp",EDGE,"E92"),sQuery(id+"F0.wireOp",EDGE,"E93"),sQuery(id+"F0.wireOp",EDGE,"E94"),sQuery(id+"F0.wireOp",EDGE,"E95"),sQuery(id+"F0.wireOp",EDGE,"E96"),sQuery(id+"F0.wireOp",EDGE,"E97"),sQuery(id+"F0.wireOp",EDGE,"E98"),sQuery(id+"F0.wireOp",EDGE,"E99"),sQuery(id+"F0.wireOp",EDGE,"E100"),sQuery(id+"F0.wireOp",EDGE,"E101"),sQuery(id+"F0.wireOp",EDGE,"E102"),sQuery(id+"F0.wireOp",EDGE,"E103"),sQuery(id+"F0.wireOp",EDGE,"E104"),sQuery(id+"F0.wireOp",EDGE,"E105"),sQuery(id+"F0.wireOp",EDGE,"E106"),sQuery(id+"F0.wireOp",EDGE,"E107"),sQuery(id+"F0.wireOp",EDGE,"E108"),sQuery(id+"F0.wireOp",EDGE,"E109"),sQuery(id+"F0.wireOp",EDGE,"E110"),sQuery(id+"F0.wireOp",EDGE,"E111"),sQuery(id+"F0.wireOp",EDGE,"E112"),sQuery(id+"F0.wireOp",EDGE,"E113"),sQuery(id+"F0.wireOp",EDGE,"E114"),sQuery(id+"F0.wireOp",EDGE,"E115"),sQuery(id+"F0.wireOp",EDGE,"E116"),sQuery(id+"F0.wireOp",EDGE,"E117"),sQuery(id+"F0.wireOp",EDGE,"E118"),sQuery(id+"F0.wireOp",EDGE,"E119"),sQuery(id+"F0.wireOp",EDGE,"E120"),sQuery(id+"F0.wireOp",EDGE,"E121"),sQuery(id+"F0.wireOp",EDGE,"E122"),sQuery(id+"F0.wireOp",EDGE,"E123"),sQuery(id+"F0.wireOp",EDGE,"E124"),sQuery(id+"F0.wireOp",EDGE,"E125"),sQuery(id+"F0.wireOp",EDGE,"E126"),sQuery(id+"F0.wireOp",EDGE,"E127"),sQuery(id+"F0.wireOp",EDGE,"E128"),sQuery(id+"F0.wireOp",EDGE,"E129"),sQuery(id+"F0.wireOp",EDGE,"E130"),sQuery(id+"F0.wireOp",EDGE,"E131"),sQuery(id+"F0.wireOp",EDGE,"E132"),sQuery(id+"F0.wireOp",EDGE,"E133"),sQuery(id+"F0.wireOp",EDGE,"E134"),sQuery(id+"F0.wireOp",EDGE,"E135"),sQuery(id+"F0.wireOp",EDGE,"E136"),sQuery(id+"F0.wireOp",EDGE,"E137"),sQuery(id+"F0.wireOp",EDGE,"E138"),sQuery(id+"F0.wireOp",EDGE,"E139"),sQuery(id+"F0.wireOp",EDGE,"E140"),sQuery(id+"F0.wireOp",EDGE,"E141"),sQuery(id+"F0.wireOp",EDGE,"E142"),sQuery(id+"F0.wireOp",EDGE,"E143"),sQuery(id+"F0.wireOp",EDGE,"E144"),sQuery(id+"F0.wireOp",EDGE,"E145"),sQuery(id+"F0.wireOp",EDGE,"E146"),sQuery(id+"F0.wireOp",EDGE,"E147"),sQuery(id+"F0.wireOp",EDGE,"E148"),sQuery(id+"F0.wireOp",EDGE,"E149"),sQuery(id+"F0.wireOp",EDGE,"E150"),sQuery(id+"F0.wireOp",EDGE,"E151"),sQuery(id+"F0.wireOp",EDGE,"E152"),sQuery(id+"F0.wireOp",EDGE,"E153"),sQuery(id+"F0.wireOp",EDGE,"E154"),sQuery(id+"F0.wireOp",EDGE,"E155"),sQuery(id+"F0.wireOp",EDGE,"E156"),sQuery(id+"F0.wireOp",EDGE,"E157"),sQuery(id+"F0.wireOp",EDGE,"E158"),sQuery(id+"F0.wireOp",EDGE,"E159"),sQuery(id+"F0.wireOp",EDGE,"E160"),sQuery(id+"F0.wireOp",EDGE,"E161"),sQuery(id+"F0.wireOp",EDGE,"E162"),sQuery(id+"F0.wireOp",EDGE,"E163"),sQuery(id+"F0.wireOp",EDGE,"E164"),sQuery(id+"F0.wireOp",EDGE,"E165"),sQuery(id+"F0.wireOp",EDGE,"E166"),sQuery(id+"F0.wireOp",EDGE,"E167"),sQuery(id+"F0.wireOp",EDGE,"E168"),sQuery(id+"F0.wireOp",EDGE,"E169"),sQuery(id+"F0.wireOp",EDGE,"E170"),sQuery(id+"F0.wireOp",EDGE,"E171"),sQuery(id+"F0.wireOp",EDGE,"E172"),sQuery(id+"F0.wireOp",EDGE,"E173"),sQuery(id+"F0.wireOp",EDGE,"E174"),sQuery(id+"F0.wireOp",EDGE,"E175"),sQuery(id+"F0.wireOp",EDGE,"E176"),sQuery(id+"F0.wireOp",EDGE,"E177"),sQuery(id+"F0.wireOp",EDGE,"E178"),sQuery(id+"F0.wireOp",EDGE,"E179"),sQuery(id+"F0.wireOp",EDGE,"E180"),sQuery(id+"F0.wireOp",EDGE,"E181"),sQuery(id+"F0.wireOp",EDGE,"E182"),sQuery(id+"F0.wireOp",EDGE,"E183"),sQuery(id+"F0.wireOp",EDGE,"E184"),sQuery(id+"F0.wireOp",EDGE,"E185"),sQuery(id+"F0.wireOp",EDGE,"E186"),sQuery(id+"F0.wireOp",EDGE,"E187"),sQuery(id+"F0.wireOp",EDGE,"E188"),sQuery(id+"F0.wireOp",EDGE,"E189"),sQuery(id+"F0.wireOp",EDGE,"E190"),sQuery(id+"F0.wireOp",EDGE,"E191"),sQuery(id+"F0.wireOp",EDGE,"E192"),sQuery(id+"F0.wireOp",EDGE,"E193"),sQuery(id+"F0.wireOp",EDGE,"E194"),sQuery(id+"F0.wireOp",EDGE,"E195"),sQuery(id+"F0.wireOp",EDGE,"E196"),sQuery(id+"F0.wireOp",EDGE,"E197"),sQuery(id+"F0.wireOp",EDGE,"E198"),sQuery(id+"F0.wireOp",EDGE,"E199"),sQuery(id+"F0.wireOp",EDGE,"E200"),sQuery(id+"F0.wireOp",EDGE,"E201"),sQuery(id+"F0.wireOp",EDGE,"E202"),sQuery(id+"F0.wireOp",EDGE,"E203"),sQuery(id+"F0.wireOp",EDGE,"E204"),sQuery(id+"F0.wireOp",EDGE,"E205"),sQuery(id+"F0.wireOp",EDGE,"E206"),sQuery(id+"F0.wireOp",EDGE,"E207"),sQuery(id+"F0.wireOp",EDGE,"E208"),sQuery(id+"F0.wireOp",EDGE,"E209"),sQuery(id+"F0.wireOp",EDGE,"E210"),sQuery(id+"F0.wireOp",EDGE,"E211"),sQuery(id+"F0.wireOp",EDGE,"E212"),sQuery(id+"F0.wireOp",EDGE,"E213"),sQuery(id+"F0.wireOp",EDGE,"E214"),sQuery(id+"F0.wireOp",EDGE,"E215"),sQuery(id+"F0.wireOp",EDGE,"E216"),sQuery(id+"F0.wireOp",EDGE,"E217"),sQuery(id+"F0.wireOp",EDGE,"E218"),sQuery(id+"F0.wireOp",EDGE,"E219"),sQuery(id+"F0.wireOp",EDGE,"E220"),sQuery(id+"F0.wireOp",EDGE,"E221"),sQuery(id+"F0.wireOp",EDGE,"E222"),sQuery(id+"F0.wireOp",EDGE,"E223"),sQuery(id+"F0.wireOp",EDGE,"E224"),sQuery(id+"F0.wireOp",EDGE,"E225"),sQuery(id+"F0.wireOp",EDGE,"E226"),sQuery(id+"F0.wireOp",EDGE,"E227"),sQuery(id+"F0.wireOp",EDGE,"E228"),sQuery(id+"F0.wireOp",EDGE,"E229"),sQuery(id+"F0.wireOp",EDGE,"E230"),sQuery(id+"F0.wireOp",EDGE,"E231"),sQuery(id+"F0.wireOp",EDGE,"E232"),sQuery(id+"F0.wireOp",EDGE,"E233"),sQuery(id+"F0.wireOp",EDGE,"E234"),sQuery(id+"F0.wireOp",EDGE,"E235"),sQuery(id+"F0.wireOp",EDGE,"E236"),sQuery(id+"F0.wireOp",EDGE,"E237"),sQuery(id+"F0.wireOp",EDGE,"E238"),sQuery(id+"F0.wireOp",EDGE,"E239"),sQuery(id+"F0.wireOp",EDGE,"E240"),sQuery(id+"F0.wireOp",EDGE,"E241"),sQuery(id+"F0.wireOp",EDGE,"E242"),sQuery(id+"F0.wireOp",EDGE,"E243"),sQuery(id+"F0.wireOp",EDGE,"E244"),sQuery(id+"F0.wireOp",EDGE,"E245"),sQuery(id+"F0.wireOp",EDGE,"E246"),sQuery(id+"F0.wireOp",EDGE,"E247"),sQuery(id+"F0.wireOp",EDGE,"E248"),sQuery(id+"F0.wireOp",EDGE,"E249"),sQuery(id+"F0.wireOp",EDGE,"E250"),sQuery(id+"F0.wireOp",EDGE,"E251"),sQuery(id+"F0.wireOp",EDGE,"E252"),sQuery(id+"F0.wireOp",EDGE,"E253"),sQuery(id+"F0.wireOp",EDGE,"E254"),sQuery(id+"F0.wireOp",EDGE,"E255"),sQuery(id+"F0.wireOp",EDGE,"E256"),sQuery(id+"F0.wireOp",EDGE,"E257"),sQuery(id+"F0.wireOp",EDGE,"E258"),sQuery(id+"F0.wireOp",EDGE,"E259"),sQuery(id+"F0.wireOp",EDGE,"E260"),sQuery(id+"F0.wireOp",EDGE,"E261"),sQuery(id+"F0.wireOp",EDGE,"E262"),sQuery(id+"F0.wireOp",EDGE,"E263"),sQuery(id+"F0.wireOp",EDGE,"E264"),sQuery(id+"F0.wireOp",EDGE,"E265"),sQuery(id+"F0.wireOp",EDGE,"E266"),sQuery(id+"F0.wireOp",EDGE,"E267"),sQuery(id+"F0.wireOp",EDGE,"E268"),sQuery(id+"F0.wireOp",EDGE,"E269"),sQuery(id+"F0.wireOp",EDGE,"E270"),sQuery(id+"F0.wireOp",EDGE,"E271"),sQuery(id+"F0.wireOp",EDGE,"E272"),sQuery(id+"F0.wireOp",EDGE,"E273"),sQuery(id+"F0.wireOp",EDGE,"E274"),sQuery(id+"F0.wireOp",EDGE,"E275"),sQuery(id+"F0.wireOp",EDGE,"E276"),sQuery(id+"F0.wireOp",EDGE,"E277"),sQuery(id+"F0.wireOp",EDGE,"E278"),sQuery(id+"F0.wireOp",EDGE,"E279"),sQuery(id+"F0.wireOp",EDGE,"E280"),sQuery(id+"F0.wireOp",EDGE,"E281"),sQuery(id+"F0.wireOp",EDGE,"E282"),sQuery(id+"F0.wireOp",EDGE,"E283"),sQuery(id+"F0.wireOp",EDGE,"E284"),sQuery(id+"F0.wireOp",EDGE,"E285"),sQuery(id+"F0.wireOp",EDGE,"E286"),sQuery(id+"F0.wireOp",EDGE,"E287"),sQuery(id+"F0.wireOp",EDGE,"E288"),sQuery(id+"F0.wireOp",EDGE,"E289"),sQuery(id+"F0.wireOp",EDGE,"E290"),sQuery(id+"F0.wireOp",EDGE,"E291"),sQuery(id+"F0.wireOp",EDGE,"E292"),sQuery(id+"F0.wireOp",EDGE,"E293"),sQuery(id+"F0.wireOp",EDGE,"E294"),sQuery(id+"F0.wireOp",EDGE,"E295"),sQuery(id+"F0.wireOp",EDGE,"E296"),sQuery(id+"F0.wireOp",EDGE,"E297"),sQuery(id+"F0.wireOp",EDGE,"E298"),sQuery(id+"F0.wireOp",EDGE,"E299"),sQuery(id+"F0.wireOp",EDGE,"E300"),sQuery(id+"F0.wireOp",EDGE,"E301"),sQuery(id+"F0.wireOp",EDGE,"E302"),sQuery(id+"F0.wireOp",EDGE,"E303"),sQuery(id+"F0.wireOp",EDGE,"E304"),sQuery(id+"F0.wireOp",EDGE,"E305"),sQuery(id+"F0.wireOp",EDGE,"E306"),sQuery(id+"F0.wireOp",EDGE,"E307"),sQuery(id+"F0.wireOp",EDGE,"E308"),sQuery(id+"F0.wireOp",EDGE,"E309"),sQuery(id+"F0.wireOp",EDGE,"E310"),sQuery(id+"F0.wireOp",EDGE,"E311"),sQuery(id+"F0.wireOp",EDGE,"E312"),sQuery(id+"F0.wireOp",EDGE,"E313"),sQuery(id+"F0.wireOp",EDGE,"E314"),sQuery(id+"F0.wireOp",EDGE,"E315"),sQuery(id+"F0.wireOp",EDGE,"E316"),sQuery(id+"F0.wireOp",EDGE,"E317"),sQuery(id+"F0.wireOp",EDGE,"E318"),sQuery(id+"F0.wireOp",EDGE,"E319"),sQuery(id+"F0.wireOp",EDGE,"E320"),sQuery(id+"F0.wireOp",EDGE,"E321"),sQuery(id+"F0.wireOp",EDGE,"E322"),sQuery(id+"F0.wireOp",EDGE,"E323"),sQuery(id+"F0.wireOp",EDGE,"E324"),sQuery(id+"F0.wireOp",EDGE,"E325"),sQuery(id+"F0.wireOp",EDGE,"E326"),sQuery(id+"F0.wireOp",EDGE,"E327"),sQuery(id+"F0.wireOp",EDGE,"E328"),sQuery(id+"F0.wireOp",EDGE,"E329"),sQuery(id+"F0.wireOp",EDGE,"E330"),sQuery(id+"F0.wireOp",EDGE,"E331"),sQuery(id+"F0.wireOp",EDGE,"E332"),sQuery(id+"F0.wireOp",EDGE,"E333"),sQuery(id+"F0.wireOp",EDGE,"E334"),sQuery(id+"F0.wireOp",EDGE,"E335"),sQuery(id+"F0.wireOp",EDGE,"E336"),sQuery(id+"F0.wireOp",EDGE,"E337"),sQuery(id+"F0.wireOp",EDGE,"E338"),sQuery(id+"F0.wireOp",EDGE,"E339"),sQuery(id+"F0.wireOp",EDGE,"E340"),sQuery(id+"F0.wireOp",EDGE,"E341"),sQuery(id+"F0.wireOp",EDGE,"E342"),sQuery(id+"F0.wireOp",EDGE,"E343"),sQuery(id+"F0.wireOp",EDGE,"E344"),sQuery(id+"F0.wireOp",EDGE,"E345"),sQuery(id+"F0.wireOp",EDGE,"E346"),sQuery(id+"F0.wireOp",EDGE,"E347"),sQuery(id+"F0.wireOp",EDGE,"E348"),sQuery(id+"F0.wireOp",EDGE,"E349"),sQuery(id+"F0.wireOp",EDGE,"E350"),sQuery(id+"F0.wireOp",EDGE,"E351"),sQuery(id+"F0.wireOp",EDGE,"E352"),sQuery(id+"F0.wireOp",EDGE,"E353"),sQuery(id+"F0.wireOp",EDGE,"E354"),sQuery(id+"F0.wireOp",EDGE,"E355"),sQuery(id+"F0.wireOp",EDGE,"E356"),sQuery(id+"F0.wireOp",EDGE,"E357"),sQuery(id+"F0.wireOp",EDGE,"E358"),sQuery(id+"F0.wireOp",EDGE,"E359"),sQuery(id+"F0.wireOp",EDGE,"5d8641b0-5a66-404d-8850-5fb83d48cf94")])]});
            transform(context, id + "F2", {"entities" : qUnion([Q0]), "transformType" : TransformType.TRANSLATION_3D, "dx" : 0 * mm, "dy" : -3 * mm, "dz" : 0 * mm, "makeCopy" : true});
        }
        {
            var Q0;
            Q0=makeQuery(id+"F1.opExtrude","SWEPT_BODY",BODY,{"disambiguationData":[OSD([sQuery(id+"F0.wireOp",EDGE,"E0"),sQuery(id+"F0.wireOp",EDGE,"E1"),sQuery(id+"F0.wireOp",EDGE,"E2"),sQuery(id+"F0.wireOp",EDGE,"E3"),sQuery(id+"F0.wireOp",EDGE,"E4"),sQuery(id+"F0.wireOp",EDGE,"E5"),sQuery(id+"F0.wireOp",EDGE,"E6"),sQuery(id+"F0.wireOp",EDGE,"E7"),sQuery(id+"F0.wireOp",EDGE,"E8"),sQuery(id+"F0.wireOp",EDGE,"E9"),sQuery(id+"F0.wireOp",EDGE,"E10"),sQuery(id+"F0.wireOp",EDGE,"E11"),sQuery(id+"F0.wireOp",EDGE,"E12"),sQuery(id+"F0.wireOp",EDGE,"E13"),sQuery(id+"F0.wireOp",EDGE,"E14"),sQuery(id+"F0.wireOp",EDGE,"E15"),sQuery(id+"F0.wireOp",EDGE,"E16"),sQuery(id+"F0.wireOp",EDGE,"E17"),sQuery(id+"F0.wireOp",EDGE,"E18"),sQuery(id+"F0.wireOp",EDGE,"E19"),sQuery(id+"F0.wireOp",EDGE,"E20"),sQuery(id+"F0.wireOp",EDGE,"E21"),sQuery(id+"F0.wireOp",EDGE,"E22"),sQuery(id+"F0.wireOp",EDGE,"E23"),sQuery(id+"F0.wireOp",EDGE,"E24"),sQuery(id+"F0.wireOp",EDGE,"E25"),sQuery(id+"F0.wireOp",EDGE,"E26"),sQuery(id+"F0.wireOp",EDGE,"E27"),sQuery(id+"F0.wireOp",EDGE,"E28"),sQuery(id+"F0.wireOp",EDGE,"E29"),sQuery(id+"F0.wireOp",EDGE,"E30"),sQuery(id+"F0.wireOp",EDGE,"E31"),sQuery(id+"F0.wireOp",EDGE,"E32"),sQuery(id+"F0.wireOp",EDGE,"E33"),sQuery(id+"F0.wireOp",EDGE,"E34"),sQuery(id+"F0.wireOp",EDGE,"E35"),sQuery(id+"F0.wireOp",EDGE,"E36"),sQuery(id+"F0.wireOp",EDGE,"E37"),sQuery(id+"F0.wireOp",EDGE,"E38"),sQuery(id+"F0.wireOp",EDGE,"E39"),sQuery(id+"F0.wireOp",EDGE,"E40"),sQuery(id+"F0.wireOp",EDGE,"E41"),sQuery(id+"F0.wireOp",EDGE,"E42"),sQuery(id+"F0.wireOp",EDGE,"E43"),sQuery(id+"F0.wireOp",EDGE,"E44"),sQuery(id+"F0.wireOp",EDGE,"E45"),sQuery(id+"F0.wireOp",EDGE,"E46"),sQuery(id+"F0.wireOp",EDGE,"E47"),sQuery(id+"F0.wireOp",EDGE,"E48"),sQuery(id+"F0.wireOp",EDGE,"E49"),sQuery(id+"F0.wireOp",EDGE,"E50"),sQuery(id+"F0.wireOp",EDGE,"E51"),sQuery(id+"F0.wireOp",EDGE,"E52"),sQuery(id+"F0.wireOp",EDGE,"E53"),sQuery(id+"F0.wireOp",EDGE,"E54"),sQuery(id+"F0.wireOp",EDGE,"E55"),sQuery(id+"F0.wireOp",EDGE,"E56"),sQuery(id+"F0.wireOp",EDGE,"E57"),sQuery(id+"F0.wireOp",EDGE,"E58"),sQuery(id+"F0.wireOp",EDGE,"E59"),sQuery(id+"F0.wireOp",EDGE,"E60"),sQuery(id+"F0.wireOp",EDGE,"E61"),sQuery(id+"F0.wireOp",EDGE,"E62"),sQuery(id+"F0.wireOp",EDGE,"E63"),sQuery(id+"F0.wireOp",EDGE,"E64"),sQuery(id+"F0.wireOp",EDGE,"E65"),sQuery(id+"F0.wireOp",EDGE,"E66"),sQuery(id+"F0.wireOp",EDGE,"E67"),sQuery(id+"F0.wireOp",EDGE,"E68"),sQuery(id+"F0.wireOp",EDGE,"E69"),sQuery(id+"F0.wireOp",EDGE,"E70"),sQuery(id+"F0.wireOp",EDGE,"E71"),sQuery(id+"F0.wireOp",EDGE,"E72"),sQuery(id+"F0.wireOp",EDGE,"E73"),sQuery(id+"F0.wireOp",EDGE,"E74"),sQuery(id+"F0.wireOp",EDGE,"E75"),sQuery(id+"F0.wireOp",EDGE,"E76"),sQuery(id+"F0.wireOp",EDGE,"E77"),sQuery(id+"F0.wireOp",EDGE,"E78"),sQuery(id+"F0.wireOp",EDGE,"E79"),sQuery(id+"F0.wireOp",EDGE,"E80"),sQuery(id+"F0.wireOp",EDGE,"E81"),sQuery(id+"F0.wireOp",EDGE,"E82"),sQuery(id+"F0.wireOp",EDGE,"E83"),sQuery(id+"F0.wireOp",EDGE,"E84"),sQuery(id+"F0.wireOp",EDGE,"E85"),sQuery(id+"F0.wireOp",EDGE,"E86"),sQuery(id+"F0.wireOp",EDGE,"E87"),sQuery(id+"F0.wireOp",EDGE,"E88"),sQuery(id+"F0.wireOp",EDGE,"E89"),sQuery(id+"F0.wireOp",EDGE,"E90"),sQuery(id+"F0.wireOp",EDGE,"E91"),sQuery(id+"F0.wireOp",EDGE,"E92"),sQuery(id+"F0.wireOp",EDGE,"E93"),sQuery(id+"F0.wireOp",EDGE,"E94"),sQuery(id+"F0.wireOp",EDGE,"E95"),sQuery(id+"F0.wireOp",EDGE,"E96"),sQuery(id+"F0.wireOp",EDGE,"E97"),sQuery(id+"F0.wireOp",EDGE,"E98"),sQuery(id+"F0.wireOp",EDGE,"E99"),sQuery(id+"F0.wireOp",EDGE,"E100"),sQuery(id+"F0.wireOp",EDGE,"E101"),sQuery(id+"F0.wireOp",EDGE,"E102"),sQuery(id+"F0.wireOp",EDGE,"E103"),sQuery(id+"F0.wireOp",EDGE,"E104"),sQuery(id+"F0.wireOp",EDGE,"E105"),sQuery(id+"F0.wireOp",EDGE,"E106"),sQuery(id+"F0.wireOp",EDGE,"E107"),sQuery(id+"F0.wireOp",EDGE,"E108"),sQuery(id+"F0.wireOp",EDGE,"E109"),sQuery(id+"F0.wireOp",EDGE,"E110"),sQuery(id+"F0.wireOp",EDGE,"E111"),sQuery(id+"F0.wireOp",EDGE,"E112"),sQuery(id+"F0.wireOp",EDGE,"E113"),sQuery(id+"F0.wireOp",EDGE,"E114"),sQuery(id+"F0.wireOp",EDGE,"E115"),sQuery(id+"F0.wireOp",EDGE,"E116"),sQuery(id+"F0.wireOp",EDGE,"E117"),sQuery(id+"F0.wireOp",EDGE,"E118"),sQuery(id+"F0.wireOp",EDGE,"E119"),sQuery(id+"F0.wireOp",EDGE,"E120"),sQuery(id+"F0.wireOp",EDGE,"E121"),sQuery(id+"F0.wireOp",EDGE,"E122"),sQuery(id+"F0.wireOp",EDGE,"E123"),sQuery(id+"F0.wireOp",EDGE,"E124"),sQuery(id+"F0.wireOp",EDGE,"E125"),sQuery(id+"F0.wireOp",EDGE,"E126"),sQuery(id+"F0.wireOp",EDGE,"E127"),sQuery(id+"F0.wireOp",EDGE,"E128"),sQuery(id+"F0.wireOp",EDGE,"E129"),sQuery(id+"F0.wireOp",EDGE,"E130"),sQuery(id+"F0.wireOp",EDGE,"E131"),sQuery(id+"F0.wireOp",EDGE,"E132"),sQuery(id+"F0.wireOp",EDGE,"E133"),sQuery(id+"F0.wireOp",EDGE,"E134"),sQuery(id+"F0.wireOp",EDGE,"E135"),sQuery(id+"F0.wireOp",EDGE,"E136"),sQuery(id+"F0.wireOp",EDGE,"E137"),sQuery(id+"F0.wireOp",EDGE,"E138"),sQuery(id+"F0.wireOp",EDGE,"E139"),sQuery(id+"F0.wireOp",EDGE,"E140"),sQuery(id+"F0.wireOp",EDGE,"E141"),sQuery(id+"F0.wireOp",EDGE,"E142"),sQuery(id+"F0.wireOp",EDGE,"E143"),sQuery(id+"F0.wireOp",EDGE,"E144"),sQuery(id+"F0.wireOp",EDGE,"E145"),sQuery(id+"F0.wireOp",EDGE,"E146"),sQuery(id+"F0.wireOp",EDGE,"E147"),sQuery(id+"F0.wireOp",EDGE,"E148"),sQuery(id+"F0.wireOp",EDGE,"E149"),sQuery(id+"F0.wireOp",EDGE,"E150"),sQuery(id+"F0.wireOp",EDGE,"E151"),sQuery(id+"F0.wireOp",EDGE,"E152"),sQuery(id+"F0.wireOp",EDGE,"E153"),sQuery(id+"F0.wireOp",EDGE,"E154"),sQuery(id+"F0.wireOp",EDGE,"E155"),sQuery(id+"F0.wireOp",EDGE,"E156"),sQuery(id+"F0.wireOp",EDGE,"E157"),sQuery(id+"F0.wireOp",EDGE,"E158"),sQuery(id+"F0.wireOp",EDGE,"E159"),sQuery(id+"F0.wireOp",EDGE,"E160"),sQuery(id+"F0.wireOp",EDGE,"E161"),sQuery(id+"F0.wireOp",EDGE,"E162"),sQuery(id+"F0.wireOp",EDGE,"E163"),sQuery(id+"F0.wireOp",EDGE,"E164"),sQuery(id+"F0.wireOp",EDGE,"E165"),sQuery(id+"F0.wireOp",EDGE,"E166"),sQuery(id+"F0.wireOp",EDGE,"E167"),sQuery(id+"F0.wireOp",EDGE,"E168"),sQuery(id+"F0.wireOp",EDGE,"E169"),sQuery(id+"F0.wireOp",EDGE,"E170"),sQuery(id+"F0.wireOp",EDGE,"E171"),sQuery(id+"F0.wireOp",EDGE,"E172"),sQuery(id+"F0.wireOp",EDGE,"E173"),sQuery(id+"F0.wireOp",EDGE,"E174"),sQuery(id+"F0.wireOp",EDGE,"E175"),sQuery(id+"F0.wireOp",EDGE,"E176"),sQuery(id+"F0.wireOp",EDGE,"E177"),sQuery(id+"F0.wireOp",EDGE,"E178"),sQuery(id+"F0.wireOp",EDGE,"E179"),sQuery(id+"F0.wireOp",EDGE,"E180"),sQuery(id+"F0.wireOp",EDGE,"E181"),sQuery(id+"F0.wireOp",EDGE,"E182"),sQuery(id+"F0.wireOp",EDGE,"E183"),sQuery(id+"F0.wireOp",EDGE,"E184"),sQuery(id+"F0.wireOp",EDGE,"E185"),sQuery(id+"F0.wireOp",EDGE,"E186"),sQuery(id+"F0.wireOp",EDGE,"E187"),sQuery(id+"F0.wireOp",EDGE,"E188"),sQuery(id+"F0.wireOp",EDGE,"E189"),sQuery(id+"F0.wireOp",EDGE,"E190"),sQuery(id+"F0.wireOp",EDGE,"E191"),sQuery(id+"F0.wireOp",EDGE,"E192"),sQuery(id+"F0.wireOp",EDGE,"E193"),sQuery(id+"F0.wireOp",EDGE,"E194"),sQuery(id+"F0.wireOp",EDGE,"E195"),sQuery(id+"F0.wireOp",EDGE,"E196"),sQuery(id+"F0.wireOp",EDGE,"E197"),sQuery(id+"F0.wireOp",EDGE,"E198"),sQuery(id+"F0.wireOp",EDGE,"E199"),sQuery(id+"F0.wireOp",EDGE,"E200"),sQuery(id+"F0.wireOp",EDGE,"E201"),sQuery(id+"F0.wireOp",EDGE,"E202"),sQuery(id+"F0.wireOp",EDGE,"E203"),sQuery(id+"F0.wireOp",EDGE,"E204"),sQuery(id+"F0.wireOp",EDGE,"E205"),sQuery(id+"F0.wireOp",EDGE,"E206"),sQuery(id+"F0.wireOp",EDGE,"E207"),sQuery(id+"F0.wireOp",EDGE,"E208"),sQuery(id+"F0.wireOp",EDGE,"E209"),sQuery(id+"F0.wireOp",EDGE,"E210"),sQuery(id+"F0.wireOp",EDGE,"E211"),sQuery(id+"F0.wireOp",EDGE,"E212"),sQuery(id+"F0.wireOp",EDGE,"E213"),sQuery(id+"F0.wireOp",EDGE,"E214"),sQuery(id+"F0.wireOp",EDGE,"E215"),sQuery(id+"F0.wireOp",EDGE,"E216"),sQuery(id+"F0.wireOp",EDGE,"E217"),sQuery(id+"F0.wireOp",EDGE,"E218"),sQuery(id+"F0.wireOp",EDGE,"E219"),sQuery(id+"F0.wireOp",EDGE,"E220"),sQuery(id+"F0.wireOp",EDGE,"E221"),sQuery(id+"F0.wireOp",EDGE,"E222"),sQuery(id+"F0.wireOp",EDGE,"E223"),sQuery(id+"F0.wireOp",EDGE,"E224"),sQuery(id+"F0.wireOp",EDGE,"E225"),sQuery(id+"F0.wireOp",EDGE,"E226"),sQuery(id+"F0.wireOp",EDGE,"E227"),sQuery(id+"F0.wireOp",EDGE,"E228"),sQuery(id+"F0.wireOp",EDGE,"E229"),sQuery(id+"F0.wireOp",EDGE,"E230"),sQuery(id+"F0.wireOp",EDGE,"E231"),sQuery(id+"F0.wireOp",EDGE,"E232"),sQuery(id+"F0.wireOp",EDGE,"E233"),sQuery(id+"F0.wireOp",EDGE,"E234"),sQuery(id+"F0.wireOp",EDGE,"E235"),sQuery(id+"F0.wireOp",EDGE,"E236"),sQuery(id+"F0.wireOp",EDGE,"E237"),sQuery(id+"F0.wireOp",EDGE,"E238"),sQuery(id+"F0.wireOp",EDGE,"E239"),sQuery(id+"F0.wireOp",EDGE,"E240"),sQuery(id+"F0.wireOp",EDGE,"E241"),sQuery(id+"F0.wireOp",EDGE,"E242"),sQuery(id+"F0.wireOp",EDGE,"E243"),sQuery(id+"F0.wireOp",EDGE,"E244"),sQuery(id+"F0.wireOp",EDGE,"E245"),sQuery(id+"F0.wireOp",EDGE,"E246"),sQuery(id+"F0.wireOp",EDGE,"E247"),sQuery(id+"F0.wireOp",EDGE,"E248"),sQuery(id+"F0.wireOp",EDGE,"E249"),sQuery(id+"F0.wireOp",EDGE,"E250"),sQuery(id+"F0.wireOp",EDGE,"E251"),sQuery(id+"F0.wireOp",EDGE,"E252"),sQuery(id+"F0.wireOp",EDGE,"E253"),sQuery(id+"F0.wireOp",EDGE,"E254"),sQuery(id+"F0.wireOp",EDGE,"E255"),sQuery(id+"F0.wireOp",EDGE,"E256"),sQuery(id+"F0.wireOp",EDGE,"E257"),sQuery(id+"F0.wireOp",EDGE,"E258"),sQuery(id+"F0.wireOp",EDGE,"E259"),sQuery(id+"F0.wireOp",EDGE,"E260"),sQuery(id+"F0.wireOp",EDGE,"E261"),sQuery(id+"F0.wireOp",EDGE,"E262"),sQuery(id+"F0.wireOp",EDGE,"E263"),sQuery(id+"F0.wireOp",EDGE,"E264"),sQuery(id+"F0.wireOp",EDGE,"E265"),sQuery(id+"F0.wireOp",EDGE,"E266"),sQuery(id+"F0.wireOp",EDGE,"E267"),sQuery(id+"F0.wireOp",EDGE,"E268"),sQuery(id+"F0.wireOp",EDGE,"E269"),sQuery(id+"F0.wireOp",EDGE,"E270"),sQuery(id+"F0.wireOp",EDGE,"E271"),sQuery(id+"F0.wireOp",EDGE,"E272"),sQuery(id+"F0.wireOp",EDGE,"E273"),sQuery(id+"F0.wireOp",EDGE,"E274"),sQuery(id+"F0.wireOp",EDGE,"E275"),sQuery(id+"F0.wireOp",EDGE,"E276"),sQuery(id+"F0.wireOp",EDGE,"E277"),sQuery(id+"F0.wireOp",EDGE,"E278"),sQuery(id+"F0.wireOp",EDGE,"E279"),sQuery(id+"F0.wireOp",EDGE,"E280"),sQuery(id+"F0.wireOp",EDGE,"E281"),sQuery(id+"F0.wireOp",EDGE,"E282"),sQuery(id+"F0.wireOp",EDGE,"E283"),sQuery(id+"F0.wireOp",EDGE,"E284"),sQuery(id+"F0.wireOp",EDGE,"E285"),sQuery(id+"F0.wireOp",EDGE,"E286"),sQuery(id+"F0.wireOp",EDGE,"E287"),sQuery(id+"F0.wireOp",EDGE,"E288"),sQuery(id+"F0.wireOp",EDGE,"E289"),sQuery(id+"F0.wireOp",EDGE,"E290"),sQuery(id+"F0.wireOp",EDGE,"E291"),sQuery(id+"F0.wireOp",EDGE,"E292"),sQuery(id+"F0.wireOp",EDGE,"E293"),sQuery(id+"F0.wireOp",EDGE,"E294"),sQuery(id+"F0.wireOp",EDGE,"E295"),sQuery(id+"F0.wireOp",EDGE,"E296"),sQuery(id+"F0.wireOp",EDGE,"E297"),sQuery(id+"F0.wireOp",EDGE,"E298"),sQuery(id+"F0.wireOp",EDGE,"E299"),sQuery(id+"F0.wireOp",EDGE,"E300"),sQuery(id+"F0.wireOp",EDGE,"E301"),sQuery(id+"F0.wireOp",EDGE,"E302"),sQuery(id+"F0.wireOp",EDGE,"E303"),sQuery(id+"F0.wireOp",EDGE,"E304"),sQuery(id+"F0.wireOp",EDGE,"E305"),sQuery(id+"F0.wireOp",EDGE,"E306"),sQuery(id+"F0.wireOp",EDGE,"E307"),sQuery(id+"F0.wireOp",EDGE,"E308"),sQuery(id+"F0.wireOp",EDGE,"E309"),sQuery(id+"F0.wireOp",EDGE,"E310"),sQuery(id+"F0.wireOp",EDGE,"E311"),sQuery(id+"F0.wireOp",EDGE,"E312"),sQuery(id+"F0.wireOp",EDGE,"E313"),sQuery(id+"F0.wireOp",EDGE,"E314"),sQuery(id+"F0.wireOp",EDGE,"E315"),sQuery(id+"F0.wireOp",EDGE,"E316"),sQuery(id+"F0.wireOp",EDGE,"E317"),sQuery(id+"F0.wireOp",EDGE,"E318"),sQuery(id+"F0.wireOp",EDGE,"E319"),sQuery(id+"F0.wireOp",EDGE,"E320"),sQuery(id+"F0.wireOp",EDGE,"E321"),sQuery(id+"F0.wireOp",EDGE,"E322"),sQuery(id+"F0.wireOp",EDGE,"E323"),sQuery(id+"F0.wireOp",EDGE,"E324"),sQuery(id+"F0.wireOp",EDGE,"E325"),sQuery(id+"F0.wireOp",EDGE,"E326"),sQuery(id+"F0.wireOp",EDGE,"E327"),sQuery(id+"F0.wireOp",EDGE,"E328"),sQuery(id+"F0.wireOp",EDGE,"E329"),sQuery(id+"F0.wireOp",EDGE,"E330"),sQuery(id+"F0.wireOp",EDGE,"E331"),sQuery(id+"F0.wireOp",EDGE,"E332"),sQuery(id+"F0.wireOp",EDGE,"E333"),sQuery(id+"F0.wireOp",EDGE,"E334"),sQuery(id+"F0.wireOp",EDGE,"E335"),sQuery(id+"F0.wireOp",EDGE,"E336"),sQuery(id+"F0.wireOp",EDGE,"E337"),sQuery(id+"F0.wireOp",EDGE,"E338"),sQuery(id+"F0.wireOp",EDGE,"E339"),sQuery(id+"F0.wireOp",EDGE,"E340"),sQuery(id+"F0.wireOp",EDGE,"E341"),sQuery(id+"F0.wireOp",EDGE,"E342"),sQuery(id+"F0.wireOp",EDGE,"E343"),sQuery(id+"F0.wireOp",EDGE,"E344"),sQuery(id+"F0.wireOp",EDGE,"E345"),sQuery(id+"F0.wireOp",EDGE,"E346"),sQuery(id+"F0.wireOp",EDGE,"E347"),sQuery(id+"F0.wireOp",EDGE,"E348"),sQuery(id+"F0.wireOp",EDGE,"E349"),sQuery(id+"F0.wireOp",EDGE,"E350"),sQuery(id+"F0.wireOp",EDGE,"E351"),sQuery(id+"F0.wireOp",EDGE,"E352"),sQuery(id+"F0.wireOp",EDGE,"E353"),sQuery(id+"F0.wireOp",EDGE,"E354"),sQuery(id+"F0.wireOp",EDGE,"E355"),sQuery(id+"F0.wireOp",EDGE,"E356"),sQuery(id+"F0.wireOp",EDGE,"E357"),sQuery(id+"F0.wireOp",EDGE,"E358"),sQuery(id+"F0.wireOp",EDGE,"E359"),sQuery(id+"F0.wireOp",EDGE,"5d8641b0-5a66-404d-8850-5fb83d48cf94")])]});
            var Q1;
            Q1=qCreatedBy(makeId("Origin.pointOp"),VERTEX);
            transform(context, id + "F3", {"entities" : qUnion([Q0]), "transformType" : TransformType.SCALE_UNIFORMLY, "scale" : 0.6, "scalePoint" : qUnion([Q1]), "makeCopy" : false});
        }
        {
            var Q0;
            Q0=makeQuery(id+"F2.opPattern","COPY",FACE,{"derivedFrom":makeQuery(id+"F1.opExtrude","CAP_FACE",FACE,{"disambiguationData":[OSD([sQuery(id+"F0.wireOp",EDGE,"E0"),sQuery(id+"F0.wireOp",EDGE,"E1"),sQuery(id+"F0.wireOp",EDGE,"E2"),sQuery(id+"F0.wireOp",EDGE,"E3"),sQuery(id+"F0.wireOp",EDGE,"E4"),sQuery(id+"F0.wireOp",EDGE,"E5"),sQuery(id+"F0.wireOp",EDGE,"E6"),sQuery(id+"F0.wireOp",EDGE,"E7"),sQuery(id+"F0.wireOp",EDGE,"E8"),sQuery(id+"F0.wireOp",EDGE,"E9"),sQuery(id+"F0.wireOp",EDGE,"E10"),sQuery(id+"F0.wireOp",EDGE,"E11"),sQuery(id+"F0.wireOp",EDGE,"E12"),sQuery(id+"F0.wireOp",EDGE,"E13"),sQuery(id+"F0.wireOp",EDGE,"E14"),sQuery(id+"F0.wireOp",EDGE,"E15"),sQuery(id+"F0.wireOp",EDGE,"E16"),sQuery(id+"F0.wireOp",EDGE,"E17"),sQuery(id+"F0.wireOp",EDGE,"E18"),sQuery(id+"F0.wireOp",EDGE,"E19"),sQuery(id+"F0.wireOp",EDGE,"E20"),sQuery(id+"F0.wireOp",EDGE,"E21"),sQuery(id+"F0.wireOp",EDGE,"E22"),sQuery(id+"F0.wireOp",EDGE,"E23"),sQuery(id+"F0.wireOp",EDGE,"E24"),sQuery(id+"F0.wireOp",EDGE,"E25"),sQuery(id+"F0.wireOp",EDGE,"E26"),sQuery(id+"F0.wireOp",EDGE,"E27"),sQuery(id+"F0.wireOp",EDGE,"E28"),sQuery(id+"F0.wireOp",EDGE,"E29"),sQuery(id+"F0.wireOp",EDGE,"E30"),sQuery(id+"F0.wireOp",EDGE,"E31"),sQuery(id+"F0.wireOp",EDGE,"E32"),sQuery(id+"F0.wireOp",EDGE,"E33"),sQuery(id+"F0.wireOp",EDGE,"E34"),sQuery(id+"F0.wireOp",EDGE,"E35"),sQuery(id+"F0.wireOp",EDGE,"E36"),sQuery(id+"F0.wireOp",EDGE,"E37"),sQuery(id+"F0.wireOp",EDGE,"E38"),sQuery(id+"F0.wireOp",EDGE,"E39"),sQuery(id+"F0.wireOp",EDGE,"E40"),sQuery(id+"F0.wireOp",EDGE,"E41"),sQuery(id+"F0.wireOp",EDGE,"E42"),sQuery(id+"F0.wireOp",EDGE,"E43"),sQuery(id+"F0.wireOp",EDGE,"E44"),sQuery(id+"F0.wireOp",EDGE,"E45"),sQuery(id+"F0.wireOp",EDGE,"E46"),sQuery(id+"F0.wireOp",EDGE,"E47"),sQuery(id+"F0.wireOp",EDGE,"E48"),sQuery(id+"F0.wireOp",EDGE,"E49"),sQuery(id+"F0.wireOp",EDGE,"E50"),sQuery(id+"F0.wireOp",EDGE,"E51"),sQuery(id+"F0.wireOp",EDGE,"E52"),sQuery(id+"F0.wireOp",EDGE,"E53"),sQuery(id+"F0.wireOp",EDGE,"E54"),sQuery(id+"F0.wireOp",EDGE,"E55"),sQuery(id+"F0.wireOp",EDGE,"E56"),sQuery(id+"F0.wireOp",EDGE,"E57"),sQuery(id+"F0.wireOp",EDGE,"E58"),sQuery(id+"F0.wireOp",EDGE,"E59"),sQuery(id+"F0.wireOp",EDGE,"E60"),sQuery(id+"F0.wireOp",EDGE,"E61"),sQuery(id+"F0.wireOp",EDGE,"E62"),sQuery(id+"F0.wireOp",EDGE,"E63"),sQuery(id+"F0.wireOp",EDGE,"E64"),sQuery(id+"F0.wireOp",EDGE,"E65"),sQuery(id+"F0.wireOp",EDGE,"E66"),sQuery(id+"F0.wireOp",EDGE,"E67"),sQuery(id+"F0.wireOp",EDGE,"E68"),sQuery(id+"F0.wireOp",EDGE,"E69"),sQuery(id+"F0.wireOp",EDGE,"E70"),sQuery(id+"F0.wireOp",EDGE,"E71"),sQuery(id+"F0.wireOp",EDGE,"E72"),sQuery(id+"F0.wireOp",EDGE,"E73"),sQuery(id+"F0.wireOp",EDGE,"E74"),sQuery(id+"F0.wireOp",EDGE,"E75"),sQuery(id+"F0.wireOp",EDGE,"E76"),sQuery(id+"F0.wireOp",EDGE,"E77"),sQuery(id+"F0.wireOp",EDGE,"E78"),sQuery(id+"F0.wireOp",EDGE,"E79"),sQuery(id+"F0.wireOp",EDGE,"E80"),sQuery(id+"F0.wireOp",EDGE,"E81"),sQuery(id+"F0.wireOp",EDGE,"E82"),sQuery(id+"F0.wireOp",EDGE,"E83"),sQuery(id+"F0.wireOp",EDGE,"E84"),sQuery(id+"F0.wireOp",EDGE,"E85"),sQuery(id+"F0.wireOp",EDGE,"E86"),sQuery(id+"F0.wireOp",EDGE,"E87"),sQuery(id+"F0.wireOp",EDGE,"E88"),sQuery(id+"F0.wireOp",EDGE,"E89"),sQuery(id+"F0.wireOp",EDGE,"E90"),sQuery(id+"F0.wireOp",EDGE,"E91"),sQuery(id+"F0.wireOp",EDGE,"E92"),sQuery(id+"F0.wireOp",EDGE,"E93"),sQuery(id+"F0.wireOp",EDGE,"E94"),sQuery(id+"F0.wireOp",EDGE,"E95"),sQuery(id+"F0.wireOp",EDGE,"E96"),sQuery(id+"F0.wireOp",EDGE,"E97"),sQuery(id+"F0.wireOp",EDGE,"E98"),sQuery(id+"F0.wireOp",EDGE,"E99"),sQuery(id+"F0.wireOp",EDGE,"E100"),sQuery(id+"F0.wireOp",EDGE,"E101"),sQuery(id+"F0.wireOp",EDGE,"E102"),sQuery(id+"F0.wireOp",EDGE,"E103"),sQuery(id+"F0.wireOp",EDGE,"E104"),sQuery(id+"F0.wireOp",EDGE,"E105"),sQuery(id+"F0.wireOp",EDGE,"E106"),sQuery(id+"F0.wireOp",EDGE,"E107"),sQuery(id+"F0.wireOp",EDGE,"E108"),sQuery(id+"F0.wireOp",EDGE,"E109"),sQuery(id+"F0.wireOp",EDGE,"E110"),sQuery(id+"F0.wireOp",EDGE,"E111"),sQuery(id+"F0.wireOp",EDGE,"E112"),sQuery(id+"F0.wireOp",EDGE,"E113"),sQuery(id+"F0.wireOp",EDGE,"E114"),sQuery(id+"F0.wireOp",EDGE,"E115"),sQuery(id+"F0.wireOp",EDGE,"E116"),sQuery(id+"F0.wireOp",EDGE,"E117"),sQuery(id+"F0.wireOp",EDGE,"E118"),sQuery(id+"F0.wireOp",EDGE,"E119"),sQuery(id+"F0.wireOp",EDGE,"E120"),sQuery(id+"F0.wireOp",EDGE,"E121"),sQuery(id+"F0.wireOp",EDGE,"E122"),sQuery(id+"F0.wireOp",EDGE,"E123"),sQuery(id+"F0.wireOp",EDGE,"E124"),sQuery(id+"F0.wireOp",EDGE,"E125"),sQuery(id+"F0.wireOp",EDGE,"E126"),sQuery(id+"F0.wireOp",EDGE,"E127"),sQuery(id+"F0.wireOp",EDGE,"E128"),sQuery(id+"F0.wireOp",EDGE,"E129"),sQuery(id+"F0.wireOp",EDGE,"E130"),sQuery(id+"F0.wireOp",EDGE,"E131"),sQuery(id+"F0.wireOp",EDGE,"E132"),sQuery(id+"F0.wireOp",EDGE,"E133"),sQuery(id+"F0.wireOp",EDGE,"E134"),sQuery(id+"F0.wireOp",EDGE,"E135"),sQuery(id+"F0.wireOp",EDGE,"E136"),sQuery(id+"F0.wireOp",EDGE,"E137"),sQuery(id+"F0.wireOp",EDGE,"E138"),sQuery(id+"F0.wireOp",EDGE,"E139"),sQuery(id+"F0.wireOp",EDGE,"E140"),sQuery(id+"F0.wireOp",EDGE,"E141"),sQuery(id+"F0.wireOp",EDGE,"E142"),sQuery(id+"F0.wireOp",EDGE,"E143"),sQuery(id+"F0.wireOp",EDGE,"E144"),sQuery(id+"F0.wireOp",EDGE,"E145"),sQuery(id+"F0.wireOp",EDGE,"E146"),sQuery(id+"F0.wireOp",EDGE,"E147"),sQuery(id+"F0.wireOp",EDGE,"E148"),sQuery(id+"F0.wireOp",EDGE,"E149"),sQuery(id+"F0.wireOp",EDGE,"E150"),sQuery(id+"F0.wireOp",EDGE,"E151"),sQuery(id+"F0.wireOp",EDGE,"E152"),sQuery(id+"F0.wireOp",EDGE,"E153"),sQuery(id+"F0.wireOp",EDGE,"E154"),sQuery(id+"F0.wireOp",EDGE,"E155"),sQuery(id+"F0.wireOp",EDGE,"E156"),sQuery(id+"F0.wireOp",EDGE,"E157"),sQuery(id+"F0.wireOp",EDGE,"E158"),sQuery(id+"F0.wireOp",EDGE,"E159"),sQuery(id+"F0.wireOp",EDGE,"E160"),sQuery(id+"F0.wireOp",EDGE,"E161"),sQuery(id+"F0.wireOp",EDGE,"E162"),sQuery(id+"F0.wireOp",EDGE,"E163"),sQuery(id+"F0.wireOp",EDGE,"E164"),sQuery(id+"F0.wireOp",EDGE,"E165"),sQuery(id+"F0.wireOp",EDGE,"E166"),sQuery(id+"F0.wireOp",EDGE,"E167"),sQuery(id+"F0.wireOp",EDGE,"E168"),sQuery(id+"F0.wireOp",EDGE,"E169"),sQuery(id+"F0.wireOp",EDGE,"E170"),sQuery(id+"F0.wireOp",EDGE,"E171"),sQuery(id+"F0.wireOp",EDGE,"E172"),sQuery(id+"F0.wireOp",EDGE,"E173"),sQuery(id+"F0.wireOp",EDGE,"E174"),sQuery(id+"F0.wireOp",EDGE,"E175"),sQuery(id+"F0.wireOp",EDGE,"E176"),sQuery(id+"F0.wireOp",EDGE,"E177"),sQuery(id+"F0.wireOp",EDGE,"E178"),sQuery(id+"F0.wireOp",EDGE,"E179"),sQuery(id+"F0.wireOp",EDGE,"E180"),sQuery(id+"F0.wireOp",EDGE,"E181"),sQuery(id+"F0.wireOp",EDGE,"E182"),sQuery(id+"F0.wireOp",EDGE,"E183"),sQuery(id+"F0.wireOp",EDGE,"E184"),sQuery(id+"F0.wireOp",EDGE,"E185"),sQuery(id+"F0.wireOp",EDGE,"E186"),sQuery(id+"F0.wireOp",EDGE,"E187"),sQuery(id+"F0.wireOp",EDGE,"E188"),sQuery(id+"F0.wireOp",EDGE,"E189"),sQuery(id+"F0.wireOp",EDGE,"E190"),sQuery(id+"F0.wireOp",EDGE,"E191"),sQuery(id+"F0.wireOp",EDGE,"E192"),sQuery(id+"F0.wireOp",EDGE,"E193"),sQuery(id+"F0.wireOp",EDGE,"E194"),sQuery(id+"F0.wireOp",EDGE,"E195"),sQuery(id+"F0.wireOp",EDGE,"E196"),sQuery(id+"F0.wireOp",EDGE,"E197"),sQuery(id+"F0.wireOp",EDGE,"E198"),sQuery(id+"F0.wireOp",EDGE,"E199"),sQuery(id+"F0.wireOp",EDGE,"E200"),sQuery(id+"F0.wireOp",EDGE,"E201"),sQuery(id+"F0.wireOp",EDGE,"E202"),sQuery(id+"F0.wireOp",EDGE,"E203"),sQuery(id+"F0.wireOp",EDGE,"E204"),sQuery(id+"F0.wireOp",EDGE,"E205"),sQuery(id+"F0.wireOp",EDGE,"E206"),sQuery(id+"F0.wireOp",EDGE,"E207"),sQuery(id+"F0.wireOp",EDGE,"E208"),sQuery(id+"F0.wireOp",EDGE,"E209"),sQuery(id+"F0.wireOp",EDGE,"E210"),sQuery(id+"F0.wireOp",EDGE,"E211"),sQuery(id+"F0.wireOp",EDGE,"E212"),sQuery(id+"F0.wireOp",EDGE,"E213"),sQuery(id+"F0.wireOp",EDGE,"E214"),sQuery(id+"F0.wireOp",EDGE,"E215"),sQuery(id+"F0.wireOp",EDGE,"E216"),sQuery(id+"F0.wireOp",EDGE,"E217"),sQuery(id+"F0.wireOp",EDGE,"E218"),sQuery(id+"F0.wireOp",EDGE,"E219"),sQuery(id+"F0.wireOp",EDGE,"E220"),sQuery(id+"F0.wireOp",EDGE,"E221"),sQuery(id+"F0.wireOp",EDGE,"E222"),sQuery(id+"F0.wireOp",EDGE,"E223"),sQuery(id+"F0.wireOp",EDGE,"E224"),sQuery(id+"F0.wireOp",EDGE,"E225"),sQuery(id+"F0.wireOp",EDGE,"E226"),sQuery(id+"F0.wireOp",EDGE,"E227"),sQuery(id+"F0.wireOp",EDGE,"E228"),sQuery(id+"F0.wireOp",EDGE,"E229"),sQuery(id+"F0.wireOp",EDGE,"E230"),sQuery(id+"F0.wireOp",EDGE,"E231"),sQuery(id+"F0.wireOp",EDGE,"E232"),sQuery(id+"F0.wireOp",EDGE,"E233"),sQuery(id+"F0.wireOp",EDGE,"E234"),sQuery(id+"F0.wireOp",EDGE,"E235"),sQuery(id+"F0.wireOp",EDGE,"E236"),sQuery(id+"F0.wireOp",EDGE,"E237"),sQuery(id+"F0.wireOp",EDGE,"E238"),sQuery(id+"F0.wireOp",EDGE,"E239"),sQuery(id+"F0.wireOp",EDGE,"E240"),sQuery(id+"F0.wireOp",EDGE,"E241"),sQuery(id+"F0.wireOp",EDGE,"E242"),sQuery(id+"F0.wireOp",EDGE,"E243"),sQuery(id+"F0.wireOp",EDGE,"E244"),sQuery(id+"F0.wireOp",EDGE,"E245"),sQuery(id+"F0.wireOp",EDGE,"E246"),sQuery(id+"F0.wireOp",EDGE,"E247"),sQuery(id+"F0.wireOp",EDGE,"E248"),sQuery(id+"F0.wireOp",EDGE,"E249"),sQuery(id+"F0.wireOp",EDGE,"E250"),sQuery(id+"F0.wireOp",EDGE,"E251"),sQuery(id+"F0.wireOp",EDGE,"E252"),sQuery(id+"F0.wireOp",EDGE,"E253"),sQuery(id+"F0.wireOp",EDGE,"E254"),sQuery(id+"F0.wireOp",EDGE,"E255"),sQuery(id+"F0.wireOp",EDGE,"E256"),sQuery(id+"F0.wireOp",EDGE,"E257"),sQuery(id+"F0.wireOp",EDGE,"E258"),sQuery(id+"F0.wireOp",EDGE,"E259"),sQuery(id+"F0.wireOp",EDGE,"E260"),sQuery(id+"F0.wireOp",EDGE,"E261"),sQuery(id+"F0.wireOp",EDGE,"E262"),sQuery(id+"F0.wireOp",EDGE,"E263"),sQuery(id+"F0.wireOp",EDGE,"E264"),sQuery(id+"F0.wireOp",EDGE,"E265"),sQuery(id+"F0.wireOp",EDGE,"E266"),sQuery(id+"F0.wireOp",EDGE,"E267"),sQuery(id+"F0.wireOp",EDGE,"E268"),sQuery(id+"F0.wireOp",EDGE,"E269"),sQuery(id+"F0.wireOp",EDGE,"E270"),sQuery(id+"F0.wireOp",EDGE,"E271"),sQuery(id+"F0.wireOp",EDGE,"E272"),sQuery(id+"F0.wireOp",EDGE,"E273"),sQuery(id+"F0.wireOp",EDGE,"E274"),sQuery(id+"F0.wireOp",EDGE,"E275"),sQuery(id+"F0.wireOp",EDGE,"E276"),sQuery(id+"F0.wireOp",EDGE,"E277"),sQuery(id+"F0.wireOp",EDGE,"E278"),sQuery(id+"F0.wireOp",EDGE,"E279"),sQuery(id+"F0.wireOp",EDGE,"E280"),sQuery(id+"F0.wireOp",EDGE,"E281"),sQuery(id+"F0.wireOp",EDGE,"E282"),sQuery(id+"F0.wireOp",EDGE,"E283"),sQuery(id+"F0.wireOp",EDGE,"E284"),sQuery(id+"F0.wireOp",EDGE,"E285"),sQuery(id+"F0.wireOp",EDGE,"E286"),sQuery(id+"F0.wireOp",EDGE,"E287"),sQuery(id+"F0.wireOp",EDGE,"E288"),sQuery(id+"F0.wireOp",EDGE,"E289"),sQuery(id+"F0.wireOp",EDGE,"E290"),sQuery(id+"F0.wireOp",EDGE,"E291"),sQuery(id+"F0.wireOp",EDGE,"E292"),sQuery(id+"F0.wireOp",EDGE,"E293"),sQuery(id+"F0.wireOp",EDGE,"E294"),sQuery(id+"F0.wireOp",EDGE,"E295"),sQuery(id+"F0.wireOp",EDGE,"E296"),sQuery(id+"F0.wireOp",EDGE,"E297"),sQuery(id+"F0.wireOp",EDGE,"E298"),sQuery(id+"F0.wireOp",EDGE,"E299"),sQuery(id+"F0.wireOp",EDGE,"E300"),sQuery(id+"F0.wireOp",EDGE,"E301"),sQuery(id+"F0.wireOp",EDGE,"E302"),sQuery(id+"F0.wireOp",EDGE,"E303"),sQuery(id+"F0.wireOp",EDGE,"E304"),sQuery(id+"F0.wireOp",EDGE,"E305"),sQuery(id+"F0.wireOp",EDGE,"E306"),sQuery(id+"F0.wireOp",EDGE,"E307"),sQuery(id+"F0.wireOp",EDGE,"E308"),sQuery(id+"F0.wireOp",EDGE,"E309"),sQuery(id+"F0.wireOp",EDGE,"E310"),sQuery(id+"F0.wireOp",EDGE,"E311"),sQuery(id+"F0.wireOp",EDGE,"E312"),sQuery(id+"F0.wireOp",EDGE,"E313"),sQuery(id+"F0.wireOp",EDGE,"E314"),sQuery(id+"F0.wireOp",EDGE,"E315"),sQuery(id+"F0.wireOp",EDGE,"E316"),sQuery(id+"F0.wireOp",EDGE,"E317"),sQuery(id+"F0.wireOp",EDGE,"E318"),sQuery(id+"F0.wireOp",EDGE,"E319"),sQuery(id+"F0.wireOp",EDGE,"E320"),sQuery(id+"F0.wireOp",EDGE,"E321"),sQuery(id+"F0.wireOp",EDGE,"E322"),sQuery(id+"F0.wireOp",EDGE,"E323"),sQuery(id+"F0.wireOp",EDGE,"E324"),sQuery(id+"F0.wireOp",EDGE,"E325"),sQuery(id+"F0.wireOp",EDGE,"E326"),sQuery(id+"F0.wireOp",EDGE,"E327"),sQuery(id+"F0.wireOp",EDGE,"E328"),sQuery(id+"F0.wireOp",EDGE,"E329"),sQuery(id+"F0.wireOp",EDGE,"E330"),sQuery(id+"F0.wireOp",EDGE,"E331"),sQuery(id+"F0.wireOp",EDGE,"E332"),sQuery(id+"F0.wireOp",EDGE,"E333"),sQuery(id+"F0.wireOp",EDGE,"E334"),sQuery(id+"F0.wireOp",EDGE,"E335"),sQuery(id+"F0.wireOp",EDGE,"E336"),sQuery(id+"F0.wireOp",EDGE,"E337"),sQuery(id+"F0.wireOp",EDGE,"E338"),sQuery(id+"F0.wireOp",EDGE,"E339"),sQuery(id+"F0.wireOp",EDGE,"E340"),sQuery(id+"F0.wireOp",EDGE,"E341"),sQuery(id+"F0.wireOp",EDGE,"E342"),sQuery(id+"F0.wireOp",EDGE,"E343"),sQuery(id+"F0.wireOp",EDGE,"E344"),sQuery(id+"F0.wireOp",EDGE,"E345"),sQuery(id+"F0.wireOp",EDGE,"E346"),sQuery(id+"F0.wireOp",EDGE,"E347"),sQuery(id+"F0.wireOp",EDGE,"E348"),sQuery(id+"F0.wireOp",EDGE,"E349"),sQuery(id+"F0.wireOp",EDGE,"E350"),sQuery(id+"F0.wireOp",EDGE,"E351"),sQuery(id+"F0.wireOp",EDGE,"E352"),sQuery(id+"F0.wireOp",EDGE,"E353"),sQuery(id+"F0.wireOp",EDGE,"E354"),sQuery(id+"F0.wireOp",EDGE,"E355"),sQuery(id+"F0.wireOp",EDGE,"E356"),sQuery(id+"F0.wireOp",EDGE,"E357"),sQuery(id+"F0.wireOp",EDGE,"E358"),sQuery(id+"F0.wireOp",EDGE,"E359"),sQuery(id+"F0.wireOp",EDGE,"5d8641b0-5a66-404d-8850-5fb83d48cf94")])],"isStart":true}),"instanceName":"1"});
            var Q1;
            Q1=makeQuery(id+"F1.opExtrude","CAP_FACE",FACE,{"disambiguationData":[OSD([sQuery(id+"F0.wireOp",EDGE,"E0"),sQuery(id+"F0.wireOp",EDGE,"E1"),sQuery(id+"F0.wireOp",EDGE,"E2"),sQuery(id+"F0.wireOp",EDGE,"E3"),sQuery(id+"F0.wireOp",EDGE,"E4"),sQuery(id+"F0.wireOp",EDGE,"E5"),sQuery(id+"F0.wireOp",EDGE,"E6"),sQuery(id+"F0.wireOp",EDGE,"E7"),sQuery(id+"F0.wireOp",EDGE,"E8"),sQuery(id+"F0.wireOp",EDGE,"E9"),sQuery(id+"F0.wireOp",EDGE,"E10"),sQuery(id+"F0.wireOp",EDGE,"E11"),sQuery(id+"F0.wireOp",EDGE,"E12"),sQuery(id+"F0.wireOp",EDGE,"E13"),sQuery(id+"F0.wireOp",EDGE,"E14"),sQuery(id+"F0.wireOp",EDGE,"E15"),sQuery(id+"F0.wireOp",EDGE,"E16"),sQuery(id+"F0.wireOp",EDGE,"E17"),sQuery(id+"F0.wireOp",EDGE,"E18"),sQuery(id+"F0.wireOp",EDGE,"E19"),sQuery(id+"F0.wireOp",EDGE,"E20"),sQuery(id+"F0.wireOp",EDGE,"E21"),sQuery(id+"F0.wireOp",EDGE,"E22"),sQuery(id+"F0.wireOp",EDGE,"E23"),sQuery(id+"F0.wireOp",EDGE,"E24"),sQuery(id+"F0.wireOp",EDGE,"E25"),sQuery(id+"F0.wireOp",EDGE,"E26"),sQuery(id+"F0.wireOp",EDGE,"E27"),sQuery(id+"F0.wireOp",EDGE,"E28"),sQuery(id+"F0.wireOp",EDGE,"E29"),sQuery(id+"F0.wireOp",EDGE,"E30"),sQuery(id+"F0.wireOp",EDGE,"E31"),sQuery(id+"F0.wireOp",EDGE,"E32"),sQuery(id+"F0.wireOp",EDGE,"E33"),sQuery(id+"F0.wireOp",EDGE,"E34"),sQuery(id+"F0.wireOp",EDGE,"E35"),sQuery(id+"F0.wireOp",EDGE,"E36"),sQuery(id+"F0.wireOp",EDGE,"E37"),sQuery(id+"F0.wireOp",EDGE,"E38"),sQuery(id+"F0.wireOp",EDGE,"E39"),sQuery(id+"F0.wireOp",EDGE,"E40"),sQuery(id+"F0.wireOp",EDGE,"E41"),sQuery(id+"F0.wireOp",EDGE,"E42"),sQuery(id+"F0.wireOp",EDGE,"E43"),sQuery(id+"F0.wireOp",EDGE,"E44"),sQuery(id+"F0.wireOp",EDGE,"E45"),sQuery(id+"F0.wireOp",EDGE,"E46"),sQuery(id+"F0.wireOp",EDGE,"E47"),sQuery(id+"F0.wireOp",EDGE,"E48"),sQuery(id+"F0.wireOp",EDGE,"E49"),sQuery(id+"F0.wireOp",EDGE,"E50"),sQuery(id+"F0.wireOp",EDGE,"E51"),sQuery(id+"F0.wireOp",EDGE,"E52"),sQuery(id+"F0.wireOp",EDGE,"E53"),sQuery(id+"F0.wireOp",EDGE,"E54"),sQuery(id+"F0.wireOp",EDGE,"E55"),sQuery(id+"F0.wireOp",EDGE,"E56"),sQuery(id+"F0.wireOp",EDGE,"E57"),sQuery(id+"F0.wireOp",EDGE,"E58"),sQuery(id+"F0.wireOp",EDGE,"E59"),sQuery(id+"F0.wireOp",EDGE,"E60"),sQuery(id+"F0.wireOp",EDGE,"E61"),sQuery(id+"F0.wireOp",EDGE,"E62"),sQuery(id+"F0.wireOp",EDGE,"E63"),sQuery(id+"F0.wireOp",EDGE,"E64"),sQuery(id+"F0.wireOp",EDGE,"E65"),sQuery(id+"F0.wireOp",EDGE,"E66"),sQuery(id+"F0.wireOp",EDGE,"E67"),sQuery(id+"F0.wireOp",EDGE,"E68"),sQuery(id+"F0.wireOp",EDGE,"E69"),sQuery(id+"F0.wireOp",EDGE,"E70"),sQuery(id+"F0.wireOp",EDGE,"E71"),sQuery(id+"F0.wireOp",EDGE,"E72"),sQuery(id+"F0.wireOp",EDGE,"E73"),sQuery(id+"F0.wireOp",EDGE,"E74"),sQuery(id+"F0.wireOp",EDGE,"E75"),sQuery(id+"F0.wireOp",EDGE,"E76"),sQuery(id+"F0.wireOp",EDGE,"E77"),sQuery(id+"F0.wireOp",EDGE,"E78"),sQuery(id+"F0.wireOp",EDGE,"E79"),sQuery(id+"F0.wireOp",EDGE,"E80"),sQuery(id+"F0.wireOp",EDGE,"E81"),sQuery(id+"F0.wireOp",EDGE,"E82"),sQuery(id+"F0.wireOp",EDGE,"E83"),sQuery(id+"F0.wireOp",EDGE,"E84"),sQuery(id+"F0.wireOp",EDGE,"E85"),sQuery(id+"F0.wireOp",EDGE,"E86"),sQuery(id+"F0.wireOp",EDGE,"E87"),sQuery(id+"F0.wireOp",EDGE,"E88"),sQuery(id+"F0.wireOp",EDGE,"E89"),sQuery(id+"F0.wireOp",EDGE,"E90"),sQuery(id+"F0.wireOp",EDGE,"E91"),sQuery(id+"F0.wireOp",EDGE,"E92"),sQuery(id+"F0.wireOp",EDGE,"E93"),sQuery(id+"F0.wireOp",EDGE,"E94"),sQuery(id+"F0.wireOp",EDGE,"E95"),sQuery(id+"F0.wireOp",EDGE,"E96"),sQuery(id+"F0.wireOp",EDGE,"E97"),sQuery(id+"F0.wireOp",EDGE,"E98"),sQuery(id+"F0.wireOp",EDGE,"E99"),sQuery(id+"F0.wireOp",EDGE,"E100"),sQuery(id+"F0.wireOp",EDGE,"E101"),sQuery(id+"F0.wireOp",EDGE,"E102"),sQuery(id+"F0.wireOp",EDGE,"E103"),sQuery(id+"F0.wireOp",EDGE,"E104"),sQuery(id+"F0.wireOp",EDGE,"E105"),sQuery(id+"F0.wireOp",EDGE,"E106"),sQuery(id+"F0.wireOp",EDGE,"E107"),sQuery(id+"F0.wireOp",EDGE,"E108"),sQuery(id+"F0.wireOp",EDGE,"E109"),sQuery(id+"F0.wireOp",EDGE,"E110"),sQuery(id+"F0.wireOp",EDGE,"E111"),sQuery(id+"F0.wireOp",EDGE,"E112"),sQuery(id+"F0.wireOp",EDGE,"E113"),sQuery(id+"F0.wireOp",EDGE,"E114"),sQuery(id+"F0.wireOp",EDGE,"E115"),sQuery(id+"F0.wireOp",EDGE,"E116"),sQuery(id+"F0.wireOp",EDGE,"E117"),sQuery(id+"F0.wireOp",EDGE,"E118"),sQuery(id+"F0.wireOp",EDGE,"E119"),sQuery(id+"F0.wireOp",EDGE,"E120"),sQuery(id+"F0.wireOp",EDGE,"E121"),sQuery(id+"F0.wireOp",EDGE,"E122"),sQuery(id+"F0.wireOp",EDGE,"E123"),sQuery(id+"F0.wireOp",EDGE,"E124"),sQuery(id+"F0.wireOp",EDGE,"E125"),sQuery(id+"F0.wireOp",EDGE,"E126"),sQuery(id+"F0.wireOp",EDGE,"E127"),sQuery(id+"F0.wireOp",EDGE,"E128"),sQuery(id+"F0.wireOp",EDGE,"E129"),sQuery(id+"F0.wireOp",EDGE,"E130"),sQuery(id+"F0.wireOp",EDGE,"E131"),sQuery(id+"F0.wireOp",EDGE,"E132"),sQuery(id+"F0.wireOp",EDGE,"E133"),sQuery(id+"F0.wireOp",EDGE,"E134"),sQuery(id+"F0.wireOp",EDGE,"E135"),sQuery(id+"F0.wireOp",EDGE,"E136"),sQuery(id+"F0.wireOp",EDGE,"E137"),sQuery(id+"F0.wireOp",EDGE,"E138"),sQuery(id+"F0.wireOp",EDGE,"E139"),sQuery(id+"F0.wireOp",EDGE,"E140"),sQuery(id+"F0.wireOp",EDGE,"E141"),sQuery(id+"F0.wireOp",EDGE,"E142"),sQuery(id+"F0.wireOp",EDGE,"E143"),sQuery(id+"F0.wireOp",EDGE,"E144"),sQuery(id+"F0.wireOp",EDGE,"E145"),sQuery(id+"F0.wireOp",EDGE,"E146"),sQuery(id+"F0.wireOp",EDGE,"E147"),sQuery(id+"F0.wireOp",EDGE,"E148"),sQuery(id+"F0.wireOp",EDGE,"E149"),sQuery(id+"F0.wireOp",EDGE,"E150"),sQuery(id+"F0.wireOp",EDGE,"E151"),sQuery(id+"F0.wireOp",EDGE,"E152"),sQuery(id+"F0.wireOp",EDGE,"E153"),sQuery(id+"F0.wireOp",EDGE,"E154"),sQuery(id+"F0.wireOp",EDGE,"E155"),sQuery(id+"F0.wireOp",EDGE,"E156"),sQuery(id+"F0.wireOp",EDGE,"E157"),sQuery(id+"F0.wireOp",EDGE,"E158"),sQuery(id+"F0.wireOp",EDGE,"E159"),sQuery(id+"F0.wireOp",EDGE,"E160"),sQuery(id+"F0.wireOp",EDGE,"E161"),sQuery(id+"F0.wireOp",EDGE,"E162"),sQuery(id+"F0.wireOp",EDGE,"E163"),sQuery(id+"F0.wireOp",EDGE,"E164"),sQuery(id+"F0.wireOp",EDGE,"E165"),sQuery(id+"F0.wireOp",EDGE,"E166"),sQuery(id+"F0.wireOp",EDGE,"E167"),sQuery(id+"F0.wireOp",EDGE,"E168"),sQuery(id+"F0.wireOp",EDGE,"E169"),sQuery(id+"F0.wireOp",EDGE,"E170"),sQuery(id+"F0.wireOp",EDGE,"E171"),sQuery(id+"F0.wireOp",EDGE,"E172"),sQuery(id+"F0.wireOp",EDGE,"E173"),sQuery(id+"F0.wireOp",EDGE,"E174"),sQuery(id+"F0.wireOp",EDGE,"E175"),sQuery(id+"F0.wireOp",EDGE,"E176"),sQuery(id+"F0.wireOp",EDGE,"E177"),sQuery(id+"F0.wireOp",EDGE,"E178"),sQuery(id+"F0.wireOp",EDGE,"E179"),sQuery(id+"F0.wireOp",EDGE,"E180"),sQuery(id+"F0.wireOp",EDGE,"E181"),sQuery(id+"F0.wireOp",EDGE,"E182"),sQuery(id+"F0.wireOp",EDGE,"E183"),sQuery(id+"F0.wireOp",EDGE,"E184"),sQuery(id+"F0.wireOp",EDGE,"E185"),sQuery(id+"F0.wireOp",EDGE,"E186"),sQuery(id+"F0.wireOp",EDGE,"E187"),sQuery(id+"F0.wireOp",EDGE,"E188"),sQuery(id+"F0.wireOp",EDGE,"E189"),sQuery(id+"F0.wireOp",EDGE,"E190"),sQuery(id+"F0.wireOp",EDGE,"E191"),sQuery(id+"F0.wireOp",EDGE,"E192"),sQuery(id+"F0.wireOp",EDGE,"E193"),sQuery(id+"F0.wireOp",EDGE,"E194"),sQuery(id+"F0.wireOp",EDGE,"E195"),sQuery(id+"F0.wireOp",EDGE,"E196"),sQuery(id+"F0.wireOp",EDGE,"E197"),sQuery(id+"F0.wireOp",EDGE,"E198"),sQuery(id+"F0.wireOp",EDGE,"E199"),sQuery(id+"F0.wireOp",EDGE,"E200"),sQuery(id+"F0.wireOp",EDGE,"E201"),sQuery(id+"F0.wireOp",EDGE,"E202"),sQuery(id+"F0.wireOp",EDGE,"E203"),sQuery(id+"F0.wireOp",EDGE,"E204"),sQuery(id+"F0.wireOp",EDGE,"E205"),sQuery(id+"F0.wireOp",EDGE,"E206"),sQuery(id+"F0.wireOp",EDGE,"E207"),sQuery(id+"F0.wireOp",EDGE,"E208"),sQuery(id+"F0.wireOp",EDGE,"E209"),sQuery(id+"F0.wireOp",EDGE,"E210"),sQuery(id+"F0.wireOp",EDGE,"E211"),sQuery(id+"F0.wireOp",EDGE,"E212"),sQuery(id+"F0.wireOp",EDGE,"E213"),sQuery(id+"F0.wireOp",EDGE,"E214"),sQuery(id+"F0.wireOp",EDGE,"E215"),sQuery(id+"F0.wireOp",EDGE,"E216"),sQuery(id+"F0.wireOp",EDGE,"E217"),sQuery(id+"F0.wireOp",EDGE,"E218"),sQuery(id+"F0.wireOp",EDGE,"E219"),sQuery(id+"F0.wireOp",EDGE,"E220"),sQuery(id+"F0.wireOp",EDGE,"E221"),sQuery(id+"F0.wireOp",EDGE,"E222"),sQuery(id+"F0.wireOp",EDGE,"E223"),sQuery(id+"F0.wireOp",EDGE,"E224"),sQuery(id+"F0.wireOp",EDGE,"E225"),sQuery(id+"F0.wireOp",EDGE,"E226"),sQuery(id+"F0.wireOp",EDGE,"E227"),sQuery(id+"F0.wireOp",EDGE,"E228"),sQuery(id+"F0.wireOp",EDGE,"E229"),sQuery(id+"F0.wireOp",EDGE,"E230"),sQuery(id+"F0.wireOp",EDGE,"E231"),sQuery(id+"F0.wireOp",EDGE,"E232"),sQuery(id+"F0.wireOp",EDGE,"E233"),sQuery(id+"F0.wireOp",EDGE,"E234"),sQuery(id+"F0.wireOp",EDGE,"E235"),sQuery(id+"F0.wireOp",EDGE,"E236"),sQuery(id+"F0.wireOp",EDGE,"E237"),sQuery(id+"F0.wireOp",EDGE,"E238"),sQuery(id+"F0.wireOp",EDGE,"E239"),sQuery(id+"F0.wireOp",EDGE,"E240"),sQuery(id+"F0.wireOp",EDGE,"E241"),sQuery(id+"F0.wireOp",EDGE,"E242"),sQuery(id+"F0.wireOp",EDGE,"E243"),sQuery(id+"F0.wireOp",EDGE,"E244"),sQuery(id+"F0.wireOp",EDGE,"E245"),sQuery(id+"F0.wireOp",EDGE,"E246"),sQuery(id+"F0.wireOp",EDGE,"E247"),sQuery(id+"F0.wireOp",EDGE,"E248"),sQuery(id+"F0.wireOp",EDGE,"E249"),sQuery(id+"F0.wireOp",EDGE,"E250"),sQuery(id+"F0.wireOp",EDGE,"E251"),sQuery(id+"F0.wireOp",EDGE,"E252"),sQuery(id+"F0.wireOp",EDGE,"E253"),sQuery(id+"F0.wireOp",EDGE,"E254"),sQuery(id+"F0.wireOp",EDGE,"E255"),sQuery(id+"F0.wireOp",EDGE,"E256"),sQuery(id+"F0.wireOp",EDGE,"E257"),sQuery(id+"F0.wireOp",EDGE,"E258"),sQuery(id+"F0.wireOp",EDGE,"E259"),sQuery(id+"F0.wireOp",EDGE,"E260"),sQuery(id+"F0.wireOp",EDGE,"E261"),sQuery(id+"F0.wireOp",EDGE,"E262"),sQuery(id+"F0.wireOp",EDGE,"E263"),sQuery(id+"F0.wireOp",EDGE,"E264"),sQuery(id+"F0.wireOp",EDGE,"E265"),sQuery(id+"F0.wireOp",EDGE,"E266"),sQuery(id+"F0.wireOp",EDGE,"E267"),sQuery(id+"F0.wireOp",EDGE,"E268"),sQuery(id+"F0.wireOp",EDGE,"E269"),sQuery(id+"F0.wireOp",EDGE,"E270"),sQuery(id+"F0.wireOp",EDGE,"E271"),sQuery(id+"F0.wireOp",EDGE,"E272"),sQuery(id+"F0.wireOp",EDGE,"E273"),sQuery(id+"F0.wireOp",EDGE,"E274"),sQuery(id+"F0.wireOp",EDGE,"E275"),sQuery(id+"F0.wireOp",EDGE,"E276"),sQuery(id+"F0.wireOp",EDGE,"E277"),sQuery(id+"F0.wireOp",EDGE,"E278"),sQuery(id+"F0.wireOp",EDGE,"E279"),sQuery(id+"F0.wireOp",EDGE,"E280"),sQuery(id+"F0.wireOp",EDGE,"E281"),sQuery(id+"F0.wireOp",EDGE,"E282"),sQuery(id+"F0.wireOp",EDGE,"E283"),sQuery(id+"F0.wireOp",EDGE,"E284"),sQuery(id+"F0.wireOp",EDGE,"E285"),sQuery(id+"F0.wireOp",EDGE,"E286"),sQuery(id+"F0.wireOp",EDGE,"E287"),sQuery(id+"F0.wireOp",EDGE,"E288"),sQuery(id+"F0.wireOp",EDGE,"E289"),sQuery(id+"F0.wireOp",EDGE,"E290"),sQuery(id+"F0.wireOp",EDGE,"E291"),sQuery(id+"F0.wireOp",EDGE,"E292"),sQuery(id+"F0.wireOp",EDGE,"E293"),sQuery(id+"F0.wireOp",EDGE,"E294"),sQuery(id+"F0.wireOp",EDGE,"E295"),sQuery(id+"F0.wireOp",EDGE,"E296"),sQuery(id+"F0.wireOp",EDGE,"E297"),sQuery(id+"F0.wireOp",EDGE,"E298"),sQuery(id+"F0.wireOp",EDGE,"E299"),sQuery(id+"F0.wireOp",EDGE,"E300"),sQuery(id+"F0.wireOp",EDGE,"E301"),sQuery(id+"F0.wireOp",EDGE,"E302"),sQuery(id+"F0.wireOp",EDGE,"E303"),sQuery(id+"F0.wireOp",EDGE,"E304"),sQuery(id+"F0.wireOp",EDGE,"E305"),sQuery(id+"F0.wireOp",EDGE,"E306"),sQuery(id+"F0.wireOp",EDGE,"E307"),sQuery(id+"F0.wireOp",EDGE,"E308"),sQuery(id+"F0.wireOp",EDGE,"E309"),sQuery(id+"F0.wireOp",EDGE,"E310"),sQuery(id+"F0.wireOp",EDGE,"E311"),sQuery(id+"F0.wireOp",EDGE,"E312"),sQuery(id+"F0.wireOp",EDGE,"E313"),sQuery(id+"F0.wireOp",EDGE,"E314"),sQuery(id+"F0.wireOp",EDGE,"E315"),sQuery(id+"F0.wireOp",EDGE,"E316"),sQuery(id+"F0.wireOp",EDGE,"E317"),sQuery(id+"F0.wireOp",EDGE,"E318"),sQuery(id+"F0.wireOp",EDGE,"E319"),sQuery(id+"F0.wireOp",EDGE,"E320"),sQuery(id+"F0.wireOp",EDGE,"E321"),sQuery(id+"F0.wireOp",EDGE,"E322"),sQuery(id+"F0.wireOp",EDGE,"E323"),sQuery(id+"F0.wireOp",EDGE,"E324"),sQuery(id+"F0.wireOp",EDGE,"E325"),sQuery(id+"F0.wireOp",EDGE,"E326"),sQuery(id+"F0.wireOp",EDGE,"E327"),sQuery(id+"F0.wireOp",EDGE,"E328"),sQuery(id+"F0.wireOp",EDGE,"E329"),sQuery(id+"F0.wireOp",EDGE,"E330"),sQuery(id+"F0.wireOp",EDGE,"E331"),sQuery(id+"F0.wireOp",EDGE,"E332"),sQuery(id+"F0.wireOp",EDGE,"E333"),sQuery(id+"F0.wireOp",EDGE,"E334"),sQuery(id+"F0.wireOp",EDGE,"E335"),sQuery(id+"F0.wireOp",EDGE,"E336"),sQuery(id+"F0.wireOp",EDGE,"E337"),sQuery(id+"F0.wireOp",EDGE,"E338"),sQuery(id+"F0.wireOp",EDGE,"E339"),sQuery(id+"F0.wireOp",EDGE,"E340"),sQuery(id+"F0.wireOp",EDGE,"E341"),sQuery(id+"F0.wireOp",EDGE,"E342"),sQuery(id+"F0.wireOp",EDGE,"E343"),sQuery(id+"F0.wireOp",EDGE,"E344"),sQuery(id+"F0.wireOp",EDGE,"E345"),sQuery(id+"F0.wireOp",EDGE,"E346"),sQuery(id+"F0.wireOp",EDGE,"E347"),sQuery(id+"F0.wireOp",EDGE,"E348"),sQuery(id+"F0.wireOp",EDGE,"E349"),sQuery(id+"F0.wireOp",EDGE,"E350"),sQuery(id+"F0.wireOp",EDGE,"E351"),sQuery(id+"F0.wireOp",EDGE,"E352"),sQuery(id+"F0.wireOp",EDGE,"E353"),sQuery(id+"F0.wireOp",EDGE,"E354"),sQuery(id+"F0.wireOp",EDGE,"E355"),sQuery(id+"F0.wireOp",EDGE,"E356"),sQuery(id+"F0.wireOp",EDGE,"E357"),sQuery(id+"F0.wireOp",EDGE,"E358"),sQuery(id+"F0.wireOp",EDGE,"E359"),sQuery(id+"F0.wireOp",EDGE,"5d8641b0-5a66-404d-8850-5fb83d48cf94")])],"isStart":false});
            loft(context, id + "F4", {"sheetProfilesArray" : [{ "sheetProfileEntities" : qUnion([Q0]) }, { "sheetProfileEntities" : qUnion([Q1]) }]});
        }
        {
            var Q0;
            Q0=makeQuery(id+"F1.opExtrude","CAP_FACE",FACE,{"disambiguationData":[OSD([sQuery(id+"F0.wireOp",EDGE,"E0"),sQuery(id+"F0.wireOp",EDGE,"E1"),sQuery(id+"F0.wireOp",EDGE,"E2"),sQuery(id+"F0.wireOp",EDGE,"E3"),sQuery(id+"F0.wireOp",EDGE,"E4"),sQuery(id+"F0.wireOp",EDGE,"E5"),sQuery(id+"F0.wireOp",EDGE,"E6"),sQuery(id+"F0.wireOp",EDGE,"E7"),sQuery(id+"F0.wireOp",EDGE,"E8"),sQuery(id+"F0.wireOp",EDGE,"E9"),sQuery(id+"F0.wireOp",EDGE,"E10"),sQuery(id+"F0.wireOp",EDGE,"E11"),sQuery(id+"F0.wireOp",EDGE,"E12"),sQuery(id+"F0.wireOp",EDGE,"E13"),sQuery(id+"F0.wireOp",EDGE,"E14"),sQuery(id+"F0.wireOp",EDGE,"E15"),sQuery(id+"F0.wireOp",EDGE,"E16"),sQuery(id+"F0.wireOp",EDGE,"E17"),sQuery(id+"F0.wireOp",EDGE,"E18"),sQuery(id+"F0.wireOp",EDGE,"E19"),sQuery(id+"F0.wireOp",EDGE,"E20"),sQuery(id+"F0.wireOp",EDGE,"E21"),sQuery(id+"F0.wireOp",EDGE,"E22"),sQuery(id+"F0.wireOp",EDGE,"E23"),sQuery(id+"F0.wireOp",EDGE,"E24"),sQuery(id+"F0.wireOp",EDGE,"E25"),sQuery(id+"F0.wireOp",EDGE,"E26"),sQuery(id+"F0.wireOp",EDGE,"E27"),sQuery(id+"F0.wireOp",EDGE,"E28"),sQuery(id+"F0.wireOp",EDGE,"E29"),sQuery(id+"F0.wireOp",EDGE,"E30"),sQuery(id+"F0.wireOp",EDGE,"E31"),sQuery(id+"F0.wireOp",EDGE,"E32"),sQuery(id+"F0.wireOp",EDGE,"E33"),sQuery(id+"F0.wireOp",EDGE,"E34"),sQuery(id+"F0.wireOp",EDGE,"E35"),sQuery(id+"F0.wireOp",EDGE,"E36"),sQuery(id+"F0.wireOp",EDGE,"E37"),sQuery(id+"F0.wireOp",EDGE,"E38"),sQuery(id+"F0.wireOp",EDGE,"E39"),sQuery(id+"F0.wireOp",EDGE,"E40"),sQuery(id+"F0.wireOp",EDGE,"E41"),sQuery(id+"F0.wireOp",EDGE,"E42"),sQuery(id+"F0.wireOp",EDGE,"E43"),sQuery(id+"F0.wireOp",EDGE,"E44"),sQuery(id+"F0.wireOp",EDGE,"E45"),sQuery(id+"F0.wireOp",EDGE,"E46"),sQuery(id+"F0.wireOp",EDGE,"E47"),sQuery(id+"F0.wireOp",EDGE,"E48"),sQuery(id+"F0.wireOp",EDGE,"E49"),sQuery(id+"F0.wireOp",EDGE,"E50"),sQuery(id+"F0.wireOp",EDGE,"E51"),sQuery(id+"F0.wireOp",EDGE,"E52"),sQuery(id+"F0.wireOp",EDGE,"E53"),sQuery(id+"F0.wireOp",EDGE,"E54"),sQuery(id+"F0.wireOp",EDGE,"E55"),sQuery(id+"F0.wireOp",EDGE,"E56"),sQuery(id+"F0.wireOp",EDGE,"E57"),sQuery(id+"F0.wireOp",EDGE,"E58"),sQuery(id+"F0.wireOp",EDGE,"E59"),sQuery(id+"F0.wireOp",EDGE,"E60"),sQuery(id+"F0.wireOp",EDGE,"E61"),sQuery(id+"F0.wireOp",EDGE,"E62"),sQuery(id+"F0.wireOp",EDGE,"E63"),sQuery(id+"F0.wireOp",EDGE,"E64"),sQuery(id+"F0.wireOp",EDGE,"E65"),sQuery(id+"F0.wireOp",EDGE,"E66"),sQuery(id+"F0.wireOp",EDGE,"E67"),sQuery(id+"F0.wireOp",EDGE,"E68"),sQuery(id+"F0.wireOp",EDGE,"E69"),sQuery(id+"F0.wireOp",EDGE,"E70"),sQuery(id+"F0.wireOp",EDGE,"E71"),sQuery(id+"F0.wireOp",EDGE,"E72"),sQuery(id+"F0.wireOp",EDGE,"E73"),sQuery(id+"F0.wireOp",EDGE,"E74"),sQuery(id+"F0.wireOp",EDGE,"E75"),sQuery(id+"F0.wireOp",EDGE,"E76"),sQuery(id+"F0.wireOp",EDGE,"E77"),sQuery(id+"F0.wireOp",EDGE,"E78"),sQuery(id+"F0.wireOp",EDGE,"E79"),sQuery(id+"F0.wireOp",EDGE,"E80"),sQuery(id+"F0.wireOp",EDGE,"E81"),sQuery(id+"F0.wireOp",EDGE,"E82"),sQuery(id+"F0.wireOp",EDGE,"E83"),sQuery(id+"F0.wireOp",EDGE,"E84"),sQuery(id+"F0.wireOp",EDGE,"E85"),sQuery(id+"F0.wireOp",EDGE,"E86"),sQuery(id+"F0.wireOp",EDGE,"E87"),sQuery(id+"F0.wireOp",EDGE,"E88"),sQuery(id+"F0.wireOp",EDGE,"E89"),sQuery(id+"F0.wireOp",EDGE,"E90"),sQuery(id+"F0.wireOp",EDGE,"E91"),sQuery(id+"F0.wireOp",EDGE,"E92"),sQuery(id+"F0.wireOp",EDGE,"E93"),sQuery(id+"F0.wireOp",EDGE,"E94"),sQuery(id+"F0.wireOp",EDGE,"E95"),sQuery(id+"F0.wireOp",EDGE,"E96"),sQuery(id+"F0.wireOp",EDGE,"E97"),sQuery(id+"F0.wireOp",EDGE,"E98"),sQuery(id+"F0.wireOp",EDGE,"E99"),sQuery(id+"F0.wireOp",EDGE,"E100"),sQuery(id+"F0.wireOp",EDGE,"E101"),sQuery(id+"F0.wireOp",EDGE,"E102"),sQuery(id+"F0.wireOp",EDGE,"E103"),sQuery(id+"F0.wireOp",EDGE,"E104"),sQuery(id+"F0.wireOp",EDGE,"E105"),sQuery(id+"F0.wireOp",EDGE,"E106"),sQuery(id+"F0.wireOp",EDGE,"E107"),sQuery(id+"F0.wireOp",EDGE,"E108"),sQuery(id+"F0.wireOp",EDGE,"E109"),sQuery(id+"F0.wireOp",EDGE,"E110"),sQuery(id+"F0.wireOp",EDGE,"E111"),sQuery(id+"F0.wireOp",EDGE,"E112"),sQuery(id+"F0.wireOp",EDGE,"E113"),sQuery(id+"F0.wireOp",EDGE,"E114"),sQuery(id+"F0.wireOp",EDGE,"E115"),sQuery(id+"F0.wireOp",EDGE,"E116"),sQuery(id+"F0.wireOp",EDGE,"E117"),sQuery(id+"F0.wireOp",EDGE,"E118"),sQuery(id+"F0.wireOp",EDGE,"E119"),sQuery(id+"F0.wireOp",EDGE,"E120"),sQuery(id+"F0.wireOp",EDGE,"E121"),sQuery(id+"F0.wireOp",EDGE,"E122"),sQuery(id+"F0.wireOp",EDGE,"E123"),sQuery(id+"F0.wireOp",EDGE,"E124"),sQuery(id+"F0.wireOp",EDGE,"E125"),sQuery(id+"F0.wireOp",EDGE,"E126"),sQuery(id+"F0.wireOp",EDGE,"E127"),sQuery(id+"F0.wireOp",EDGE,"E128"),sQuery(id+"F0.wireOp",EDGE,"E129"),sQuery(id+"F0.wireOp",EDGE,"E130"),sQuery(id+"F0.wireOp",EDGE,"E131"),sQuery(id+"F0.wireOp",EDGE,"E132"),sQuery(id+"F0.wireOp",EDGE,"E133"),sQuery(id+"F0.wireOp",EDGE,"E134"),sQuery(id+"F0.wireOp",EDGE,"E135"),sQuery(id+"F0.wireOp",EDGE,"E136"),sQuery(id+"F0.wireOp",EDGE,"E137"),sQuery(id+"F0.wireOp",EDGE,"E138"),sQuery(id+"F0.wireOp",EDGE,"E139"),sQuery(id+"F0.wireOp",EDGE,"E140"),sQuery(id+"F0.wireOp",EDGE,"E141"),sQuery(id+"F0.wireOp",EDGE,"E142"),sQuery(id+"F0.wireOp",EDGE,"E143"),sQuery(id+"F0.wireOp",EDGE,"E144"),sQuery(id+"F0.wireOp",EDGE,"E145"),sQuery(id+"F0.wireOp",EDGE,"E146"),sQuery(id+"F0.wireOp",EDGE,"E147"),sQuery(id+"F0.wireOp",EDGE,"E148"),sQuery(id+"F0.wireOp",EDGE,"E149"),sQuery(id+"F0.wireOp",EDGE,"E150"),sQuery(id+"F0.wireOp",EDGE,"E151"),sQuery(id+"F0.wireOp",EDGE,"E152"),sQuery(id+"F0.wireOp",EDGE,"E153"),sQuery(id+"F0.wireOp",EDGE,"E154"),sQuery(id+"F0.wireOp",EDGE,"E155"),sQuery(id+"F0.wireOp",EDGE,"E156"),sQuery(id+"F0.wireOp",EDGE,"E157"),sQuery(id+"F0.wireOp",EDGE,"E158"),sQuery(id+"F0.wireOp",EDGE,"E159"),sQuery(id+"F0.wireOp",EDGE,"E160"),sQuery(id+"F0.wireOp",EDGE,"E161"),sQuery(id+"F0.wireOp",EDGE,"E162"),sQuery(id+"F0.wireOp",EDGE,"E163"),sQuery(id+"F0.wireOp",EDGE,"E164"),sQuery(id+"F0.wireOp",EDGE,"E165"),sQuery(id+"F0.wireOp",EDGE,"E166"),sQuery(id+"F0.wireOp",EDGE,"E167"),sQuery(id+"F0.wireOp",EDGE,"E168"),sQuery(id+"F0.wireOp",EDGE,"E169"),sQuery(id+"F0.wireOp",EDGE,"E170"),sQuery(id+"F0.wireOp",EDGE,"E171"),sQuery(id+"F0.wireOp",EDGE,"E172"),sQuery(id+"F0.wireOp",EDGE,"E173"),sQuery(id+"F0.wireOp",EDGE,"E174"),sQuery(id+"F0.wireOp",EDGE,"E175"),sQuery(id+"F0.wireOp",EDGE,"E176"),sQuery(id+"F0.wireOp",EDGE,"E177"),sQuery(id+"F0.wireOp",EDGE,"E178"),sQuery(id+"F0.wireOp",EDGE,"E179"),sQuery(id+"F0.wireOp",EDGE,"E180"),sQuery(id+"F0.wireOp",EDGE,"E181"),sQuery(id+"F0.wireOp",EDGE,"E182"),sQuery(id+"F0.wireOp",EDGE,"E183"),sQuery(id+"F0.wireOp",EDGE,"E184"),sQuery(id+"F0.wireOp",EDGE,"E185"),sQuery(id+"F0.wireOp",EDGE,"E186"),sQuery(id+"F0.wireOp",EDGE,"E187"),sQuery(id+"F0.wireOp",EDGE,"E188"),sQuery(id+"F0.wireOp",EDGE,"E189"),sQuery(id+"F0.wireOp",EDGE,"E190"),sQuery(id+"F0.wireOp",EDGE,"E191"),sQuery(id+"F0.wireOp",EDGE,"E192"),sQuery(id+"F0.wireOp",EDGE,"E193"),sQuery(id+"F0.wireOp",EDGE,"E194"),sQuery(id+"F0.wireOp",EDGE,"E195"),sQuery(id+"F0.wireOp",EDGE,"E196"),sQuery(id+"F0.wireOp",EDGE,"E197"),sQuery(id+"F0.wireOp",EDGE,"E198"),sQuery(id+"F0.wireOp",EDGE,"E199"),sQuery(id+"F0.wireOp",EDGE,"E200"),sQuery(id+"F0.wireOp",EDGE,"E201"),sQuery(id+"F0.wireOp",EDGE,"E202"),sQuery(id+"F0.wireOp",EDGE,"E203"),sQuery(id+"F0.wireOp",EDGE,"E204"),sQuery(id+"F0.wireOp",EDGE,"E205"),sQuery(id+"F0.wireOp",EDGE,"E206"),sQuery(id+"F0.wireOp",EDGE,"E207"),sQuery(id+"F0.wireOp",EDGE,"E208"),sQuery(id+"F0.wireOp",EDGE,"E209"),sQuery(id+"F0.wireOp",EDGE,"E210"),sQuery(id+"F0.wireOp",EDGE,"E211"),sQuery(id+"F0.wireOp",EDGE,"E212"),sQuery(id+"F0.wireOp",EDGE,"E213"),sQuery(id+"F0.wireOp",EDGE,"E214"),sQuery(id+"F0.wireOp",EDGE,"E215"),sQuery(id+"F0.wireOp",EDGE,"E216"),sQuery(id+"F0.wireOp",EDGE,"E217"),sQuery(id+"F0.wireOp",EDGE,"E218"),sQuery(id+"F0.wireOp",EDGE,"E219"),sQuery(id+"F0.wireOp",EDGE,"E220"),sQuery(id+"F0.wireOp",EDGE,"E221"),sQuery(id+"F0.wireOp",EDGE,"E222"),sQuery(id+"F0.wireOp",EDGE,"E223"),sQuery(id+"F0.wireOp",EDGE,"E224"),sQuery(id+"F0.wireOp",EDGE,"E225"),sQuery(id+"F0.wireOp",EDGE,"E226"),sQuery(id+"F0.wireOp",EDGE,"E227"),sQuery(id+"F0.wireOp",EDGE,"E228"),sQuery(id+"F0.wireOp",EDGE,"E229"),sQuery(id+"F0.wireOp",EDGE,"E230"),sQuery(id+"F0.wireOp",EDGE,"E231"),sQuery(id+"F0.wireOp",EDGE,"E232"),sQuery(id+"F0.wireOp",EDGE,"E233"),sQuery(id+"F0.wireOp",EDGE,"E234"),sQuery(id+"F0.wireOp",EDGE,"E235"),sQuery(id+"F0.wireOp",EDGE,"E236"),sQuery(id+"F0.wireOp",EDGE,"E237"),sQuery(id+"F0.wireOp",EDGE,"E238"),sQuery(id+"F0.wireOp",EDGE,"E239"),sQuery(id+"F0.wireOp",EDGE,"E240"),sQuery(id+"F0.wireOp",EDGE,"E241"),sQuery(id+"F0.wireOp",EDGE,"E242"),sQuery(id+"F0.wireOp",EDGE,"E243"),sQuery(id+"F0.wireOp",EDGE,"E244"),sQuery(id+"F0.wireOp",EDGE,"E245"),sQuery(id+"F0.wireOp",EDGE,"E246"),sQuery(id+"F0.wireOp",EDGE,"E247"),sQuery(id+"F0.wireOp",EDGE,"E248"),sQuery(id+"F0.wireOp",EDGE,"E249"),sQuery(id+"F0.wireOp",EDGE,"E250"),sQuery(id+"F0.wireOp",EDGE,"E251"),sQuery(id+"F0.wireOp",EDGE,"E252"),sQuery(id+"F0.wireOp",EDGE,"E253"),sQuery(id+"F0.wireOp",EDGE,"E254"),sQuery(id+"F0.wireOp",EDGE,"E255"),sQuery(id+"F0.wireOp",EDGE,"E256"),sQuery(id+"F0.wireOp",EDGE,"E257"),sQuery(id+"F0.wireOp",EDGE,"E258"),sQuery(id+"F0.wireOp",EDGE,"E259"),sQuery(id+"F0.wireOp",EDGE,"E260"),sQuery(id+"F0.wireOp",EDGE,"E261"),sQuery(id+"F0.wireOp",EDGE,"E262"),sQuery(id+"F0.wireOp",EDGE,"E263"),sQuery(id+"F0.wireOp",EDGE,"E264"),sQuery(id+"F0.wireOp",EDGE,"E265"),sQuery(id+"F0.wireOp",EDGE,"E266"),sQuery(id+"F0.wireOp",EDGE,"E267"),sQuery(id+"F0.wireOp",EDGE,"E268"),sQuery(id+"F0.wireOp",EDGE,"E269"),sQuery(id+"F0.wireOp",EDGE,"E270"),sQuery(id+"F0.wireOp",EDGE,"E271"),sQuery(id+"F0.wireOp",EDGE,"E272"),sQuery(id+"F0.wireOp",EDGE,"E273"),sQuery(id+"F0.wireOp",EDGE,"E274"),sQuery(id+"F0.wireOp",EDGE,"E275"),sQuery(id+"F0.wireOp",EDGE,"E276"),sQuery(id+"F0.wireOp",EDGE,"E277"),sQuery(id+"F0.wireOp",EDGE,"E278"),sQuery(id+"F0.wireOp",EDGE,"E279"),sQuery(id+"F0.wireOp",EDGE,"E280"),sQuery(id+"F0.wireOp",EDGE,"E281"),sQuery(id+"F0.wireOp",EDGE,"E282"),sQuery(id+"F0.wireOp",EDGE,"E283"),sQuery(id+"F0.wireOp",EDGE,"E284"),sQuery(id+"F0.wireOp",EDGE,"E285"),sQuery(id+"F0.wireOp",EDGE,"E286"),sQuery(id+"F0.wireOp",EDGE,"E287"),sQuery(id+"F0.wireOp",EDGE,"E288"),sQuery(id+"F0.wireOp",EDGE,"E289"),sQuery(id+"F0.wireOp",EDGE,"E290"),sQuery(id+"F0.wireOp",EDGE,"E291"),sQuery(id+"F0.wireOp",EDGE,"E292"),sQuery(id+"F0.wireOp",EDGE,"E293"),sQuery(id+"F0.wireOp",EDGE,"E294"),sQuery(id+"F0.wireOp",EDGE,"E295"),sQuery(id+"F0.wireOp",EDGE,"E296"),sQuery(id+"F0.wireOp",EDGE,"E297"),sQuery(id+"F0.wireOp",EDGE,"E298"),sQuery(id+"F0.wireOp",EDGE,"E299"),sQuery(id+"F0.wireOp",EDGE,"E300"),sQuery(id+"F0.wireOp",EDGE,"E301"),sQuery(id+"F0.wireOp",EDGE,"E302"),sQuery(id+"F0.wireOp",EDGE,"E303"),sQuery(id+"F0.wireOp",EDGE,"E304"),sQuery(id+"F0.wireOp",EDGE,"E305"),sQuery(id+"F0.wireOp",EDGE,"E306"),sQuery(id+"F0.wireOp",EDGE,"E307"),sQuery(id+"F0.wireOp",EDGE,"E308"),sQuery(id+"F0.wireOp",EDGE,"E309"),sQuery(id+"F0.wireOp",EDGE,"E310"),sQuery(id+"F0.wireOp",EDGE,"E311"),sQuery(id+"F0.wireOp",EDGE,"E312"),sQuery(id+"F0.wireOp",EDGE,"E313"),sQuery(id+"F0.wireOp",EDGE,"E314"),sQuery(id+"F0.wireOp",EDGE,"E315"),sQuery(id+"F0.wireOp",EDGE,"E316"),sQuery(id+"F0.wireOp",EDGE,"E317"),sQuery(id+"F0.wireOp",EDGE,"E318"),sQuery(id+"F0.wireOp",EDGE,"E319"),sQuery(id+"F0.wireOp",EDGE,"E320"),sQuery(id+"F0.wireOp",EDGE,"E321"),sQuery(id+"F0.wireOp",EDGE,"E322"),sQuery(id+"F0.wireOp",EDGE,"E323"),sQuery(id+"F0.wireOp",EDGE,"E324"),sQuery(id+"F0.wireOp",EDGE,"E325"),sQuery(id+"F0.wireOp",EDGE,"E326"),sQuery(id+"F0.wireOp",EDGE,"E327"),sQuery(id+"F0.wireOp",EDGE,"E328"),sQuery(id+"F0.wireOp",EDGE,"E329"),sQuery(id+"F0.wireOp",EDGE,"E330"),sQuery(id+"F0.wireOp",EDGE,"E331"),sQuery(id+"F0.wireOp",EDGE,"E332"),sQuery(id+"F0.wireOp",EDGE,"E333"),sQuery(id+"F0.wireOp",EDGE,"E334"),sQuery(id+"F0.wireOp",EDGE,"E335"),sQuery(id+"F0.wireOp",EDGE,"E336"),sQuery(id+"F0.wireOp",EDGE,"E337"),sQuery(id+"F0.wireOp",EDGE,"E338"),sQuery(id+"F0.wireOp",EDGE,"E339"),sQuery(id+"F0.wireOp",EDGE,"E340"),sQuery(id+"F0.wireOp",EDGE,"E341"),sQuery(id+"F0.wireOp",EDGE,"E342"),sQuery(id+"F0.wireOp",EDGE,"E343"),sQuery(id+"F0.wireOp",EDGE,"E344"),sQuery(id+"F0.wireOp",EDGE,"E345"),sQuery(id+"F0.wireOp",EDGE,"E346"),sQuery(id+"F0.wireOp",EDGE,"E347"),sQuery(id+"F0.wireOp",EDGE,"E348"),sQuery(id+"F0.wireOp",EDGE,"E349"),sQuery(id+"F0.wireOp",EDGE,"E350"),sQuery(id+"F0.wireOp",EDGE,"E351"),sQuery(id+"F0.wireOp",EDGE,"E352"),sQuery(id+"F0.wireOp",EDGE,"E353"),sQuery(id+"F0.wireOp",EDGE,"E354"),sQuery(id+"F0.wireOp",EDGE,"E355"),sQuery(id+"F0.wireOp",EDGE,"E356"),sQuery(id+"F0.wireOp",EDGE,"E357"),sQuery(id+"F0.wireOp",EDGE,"E358"),sQuery(id+"F0.wireOp",EDGE,"E359")])],"isStart":true});
            var sketch = newSketch(context, id + "F5", { "sketchPlane" : qUnion([Q0])});
            skCircle(sketch, "E360", {"center": v(0, 0.87) * mm, "radius": 1.96 * mm});
            skSolve(sketch);
        }
        {
            var Q0;
            Q0=makeQuery(id+"F5.imprint","IMPRINT",FACE,{"disambiguationData":[TD([[makeQuery(id+"F5.imprint","IMPRINT",EDGE,{"derivedFrom":sQuery(id+"F5.wireOp",EDGE,"E360")}),1.0]])]});
            extrude(context, id + "F6", {"entities" : qUnion([Q0]), "operationType" : NewBodyOperationType.REMOVE, "endBound" : BoundingType.THROUGH_ALL, "oppositeDirection" : true, "depth" : 5 * mm});
        }
    });
